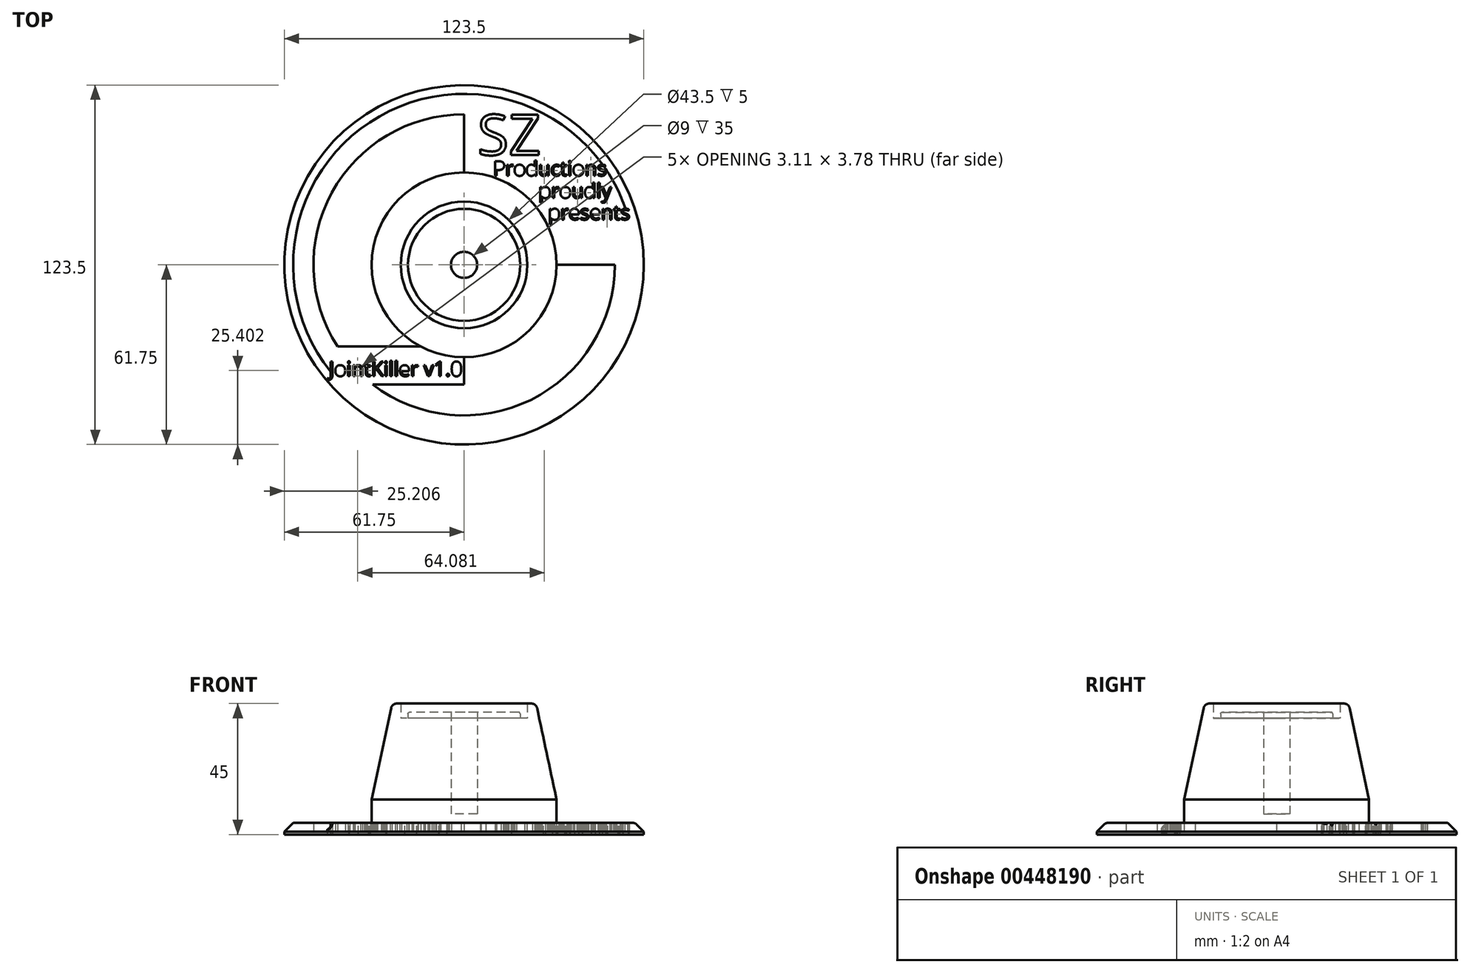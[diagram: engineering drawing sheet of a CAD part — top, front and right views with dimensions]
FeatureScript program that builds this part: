
annotation { "Feature Type Name" : "Feature", "Feature Type Description" : "" }
export const myFeature = defineFeature(function(context is Context, id is Id, definition is map)
    precondition{}
    {
        {
            var Q0;
            Q0=qCreatedBy(makeId("Top.planeOp"),FACE);
            var sketch = newSketch(context, id + "F0", { "sketchPlane" : qUnion([Q0])});
            skCircle(sketch, "E0", {"center": v(0, 0) * mm, "radius": 21.75 * mm});
            skCircle(sketch, "E1", {"center": v(0, 0) * mm, "radius": 19.25 * mm});
            skCircle(sketch, "E2", {"center": v(0, 0) * mm, "radius": 31.75 * mm});
            skCircle(sketch, "E3", {"center": v(0, 0) * mm, "radius": 61.75 * mm});
            skLineSegment(sketch, "E4", {"start": v(51.75, 0) * mm, "end": v(31.75, 0) * mm});
            skLineSegment(sketch, "E5", {"start": v(0, -51.75) * mm, "end": v(0, -31.75) * mm});
            skLineSegment(sketch, "E6", {"start": v(0, 51.75) * mm, "end": v(0, 31.75) * mm});
            skArc(sketch, "E7", {"start": v(-51.75, 0) * mm, "mid": v(-36.6, 36.6) * mm, "end": v(0, 51.75) * mm});
            skArc(sketch, "E8", {"start": v(51.75, 0) * mm, "mid": v(36.6, -36.6) * mm, "end": v(0, -51.75) * mm});
            skText(sketch, "E9", { "text": "JointKiller v1.0", "fontName": "OpenSans-Regular.ttf"});
            skCircle(sketch, "E10", {"center": v(0, 0) * mm, "radius": 4.5 * mm});
            skLineSegment(sketch, "E11.top", {"start": v(0, -41.13) * mm, "end": v(-31.4, -41.13) * mm});
            skLineSegment(sketch, "E11.left", {"start": v(0, -51.75) * mm, "end": v(0, -41.13) * mm});
            skText(sketch, "E12", { "text": "SZ", "fontName": "OpenSans-Regular.ttf"});
            skText(sketch, "E13", { "text": "Productions", "fontName": "OpenSans-Regular.ttf"});
            skText(sketch, "E14", { "text": "proudly", "fontName": "OpenSans-Regular.ttf"});
            skText(sketch, "E15", { "text": "presents\n", "fontName": "OpenSans-Regular.ttf"});
            skLineSegment(sketch, "E16.bottom", {"start": v(31.75, 0) * mm, "end": v(51.69, 0) * mm});
            skLineSegment(sketch, "E16.top", {"start": v(31.75, 12.81) * mm, "end": v(49.92, 12.81) * mm});
            skArc(sketch, "E17", {"start": v(-51.75, 0) * mm, "mid": v(-49.64, -14.61) * mm, "end": v(-43.5, -28.03) * mm});
            skLineSegment(sketch, "E18", {"start": v(31.75, 12.81) * mm, "end": v(29.05, 12.81) * mm});
            skArc(sketch, "E19", {"start": v(0, -51.75) * mm, "mid": v(-16.58, -49.02) * mm, "end": v(-31.4, -41.13) * mm});
            skArc(sketch, "E20", {"start": v(51.75, 0) * mm, "mid": v(51.35, 6.46) * mm, "end": v(50.14, 12.81) * mm});
            skLineSegment(sketch, "E21", {"start": v(-43.5, -28.03) * mm, "end": v(-14.9, -28.03) * mm});
            skLineSegment(sketch, "E22", {"start": v(0, -41.13) * mm, "end": v(22.58, -46.56) * mm});
            skLineSegment(sketch, "E23", {"start": v(28.12, -43.44) * mm, "end": v(26.04, -18.17) * mm});
            skLineSegment(sketch, "E24", {"start": v(23.6, -21.24) * mm, "end": v(22.4, -38.64) * mm});
            skLineSegment(sketch, "E25", {"start": v(22.4, -38.64) * mm, "end": v(0, -31.75) * mm});
            skLineSegment(sketch, "E26", {"start": v(-31.69, -2.02) * mm, "end": v(-51.75, 0) * mm});
            skLineSegment(sketch, "E27", {"start": v(-43.5, -28.03) * mm, "end": v(-30.77, -7.83) * mm});
            skLineSegment(sketch, "E28", {"start": v(-45.54, -24.58) * mm, "end": v(-40.29, -12.67) * mm});
            skLineSegment(sketch, "E29", {"start": v(-40.29, -12.67) * mm, "end": v(-51.15, -7.88) * mm});
            const initialGuessF0  = {"E9": [-0.0465, -0.03824, 1, 0, 0.005], "E12": [0.00463, 0.03773, 1, 0, 0.014], "E13": [0.00996, 0.03063, 1, 0, 0.005], "E14": [0.0256, 0.02298, 1, 0, 0.005], "E15": [0.0288, 0.01552, 1, 0, 0.005]};
            skSetInitialGuess(sketch, initialGuessF0);
            skSolve(sketch);
        }
        {
            var Q0;
            Q0 = qSketchRegion(id + "F0", true);
            extrude(context, id + "F1", {"entities" : qUnion([Q0]), "depth" : 4 * mm});
        }
        {
            var Q0;
            Q0=makeQuery(id+"F0.imprint","IMPRINT",FACE,{"disambiguationData":[TD([[makeQuery(id+"F0.imprint","IMPRINT",EDGE,{"derivedFrom":sQuery(id+"F0.wireOp",EDGE,"E0")}),-1.0]])]});
            extrude(context, id + "F2", {"entities" : qUnion([Q0]), "operationType" : NewBodyOperationType.ADD, "depth" : 45 * mm});
        }
        {
            var Q0;
            Q0=makeQuery(id+"F0.imprint","IMPRINT",FACE,{"disambiguationData":[TD([[makeQuery(id+"F0.imprint","IMPRINT",EDGE,{"derivedFrom":sQuery(id+"F0.wireOp",EDGE,"E0")}),1.0]])]});
            extrude(context, id + "F3", {"entities" : qUnion([Q0]), "operationType" : NewBodyOperationType.ADD, "depth" : 40 * mm});
        }
        {
            var Q0;
            Q0=makeQuery(id+"F0.imprint","IMPRINT",FACE,{"disambiguationData":[TD([[makeQuery(id+"F0.imprint","IMPRINT",EDGE,{"derivedFrom":sQuery(id+"F0.wireOp",EDGE,"E1")}),1.0]])]});
            extrude(context, id + "F4", {"entities" : qUnion([Q0]), "operationType" : NewBodyOperationType.ADD, "depth" : 42 * mm});
        }
        {
            var Q0;
            Q0=makeQuery(id+"F0.imprint","IMPRINT",FACE,{"disambiguationData":[TD([[makeQuery(id+"F0.imprint","IMPRINT",EDGE,{"derivedFrom":sQuery(id+"F0.wireOp",EDGE,"E10")}),1.0]])]});
            extrude(context, id + "F5", {"entities" : qUnion([Q0]), "operationType" : NewBodyOperationType.ADD, "depth" : 7 * mm});
        }
        {
            var Q0;
            Q0=makeQuery(id+"F2.opExtrude","CAP_EDGE",EDGE,{"disambiguationData":[OSD([sQuery(id+"F0.wireOp",EDGE,"E2")])],"isStart":false});
            chamfer(context, id + "F6", {"entities" : qUnion([Q0]), "chamferType" : ChamferType.OFFSET_ANGLE, "width" : 7 * mm, "oppositeDirection" : false, "angle" : 78 * degree, "tangentPropagation" : true});
        }
        {
            var Q0;
            {var subQ0=sQuery(id+"F0.wireOp",EDGE,"E2");Q0=makeQuery(id+"F6.opChamfer","BLEND_EDGE",EDGE,{"blendedFrom":[makeQuery(id+"F2.opExtrude","CAP_EDGE",EDGE,{"disambiguationData":[OSD([subQ0])],"isStart":false}),makeQuery(id+"F2.opExtrude","CAP_FACE",FACE,{"disambiguationData":[OSD([sQuery(id+"F0.wireOp",EDGE,"E0"),subQ0])],"isStart":false})],"blendedInto":[makeQuery(id+"F2.opExtrude","CAP_FACE",FACE,{"disambiguationData":[OSD([sQuery(id+"F0.wireOp",EDGE,"E0"),subQ0])],"isStart":false})]});}
            fillet(context, id + "F7", {"entities" : qUnion([Q0]), "radius" : 2 * mm, "tangentPropagation" : true, "allowEdgeOverflow" : false});
        }
        {
            var Q0;
            Q0=makeQuery(id+"F4.opExtrude","CAP_EDGE",EDGE,{"disambiguationData":[OSD([sQuery(id+"F0.wireOp",EDGE,"E1")])],"isStart":false});
            fillet(context, id + "F8", {"entities" : qUnion([Q0]), "radius" : 0.5 * mm, "tangentPropagation" : true, "allowEdgeOverflow" : false});
        }
        {
            var Q0;
            Q0=makeQuery(id+"F1.opExtrude","CAP_EDGE",EDGE,{"disambiguationData":[OSD([sQuery(id+"F0.wireOp",EDGE,"E3")])],"isStart":false});
            chamfer(context, id + "F9", {"entities" : qUnion([Q0]), "chamferType" : ChamferType.OFFSET_ANGLE, "width" : 3 * mm, "oppositeDirection" : false, "angle" : 45 * degree, "tangentPropagation" : true});
        }
        {
            var Q0;
            {var subQ0=sQuery(id+"F0.wireOp",EDGE,"E3");Q0=makeQuery(id+"F9.opChamfer","BLEND_EDGE",EDGE,{"disambiguationData":[OD(1.0)],"blendedFrom":[makeQuery(id+"F1.opExtrude","CAP_EDGE",EDGE,{"disambiguationData":[OSD([subQ0])],"isStart":false}),makeQuery(id+"F1.opExtrude","CAP_FACE",FACE,{"disambiguationData":[OSD([sQuery(id+"F0.wireOp",EDGE,"E2"),subQ0,sQuery(id+"F0.wireOp",EDGE,"E4"),sQuery(id+"F0.wireOp",EDGE,"E5"),sQuery(id+"F0.wireOp",EDGE,"E6"),sQuery(id+"F0.wireOp",EDGE,"E7"),sQuery(id+"F0.wireOp",EDGE,"E8"),sQuery(id+"F0.wireOp",EDGE,"E9.sketch_text.stroke-0"),sQuery(id+"F0.wireOp",EDGE,"E9.sketch_text.stroke-1"),sQuery(id+"F0.wireOp",EDGE,"E9.sketch_text.stroke-2"),sQuery(id+"F0.wireOp",EDGE,"E9.sketch_text.stroke-3"),sQuery(id+"F0.wireOp",EDGE,"E9.sketch_text.stroke-4"),sQuery(id+"F0.wireOp",EDGE,"E9.sketch_text.stroke-5"),sQuery(id+"F0.wireOp",EDGE,"E9.sketch_text.stroke-6"),sQuery(id+"F0.wireOp",EDGE,"E9.sketch_text.stroke-7"),sQuery(id+"F0.wireOp",EDGE,"E9.sketch_text.stroke-8"),sQuery(id+"F0.wireOp",EDGE,"E9.sketch_text.stroke-9"),sQuery(id+"F0.wireOp",EDGE,"E9.sketch_text.stroke-10"),sQuery(id+"F0.wireOp",EDGE,"E9.sketch_text.stroke-11"),sQuery(id+"F0.wireOp",EDGE,"E9.sketch_text.stroke-12"),sQuery(id+"F0.wireOp",EDGE,"E9.sketch_text.stroke-13"),sQuery(id+"F0.wireOp",EDGE,"E9.sketch_text.stroke-14"),sQuery(id+"F0.wireOp",EDGE,"E9.sketch_text.stroke-15"),sQuery(id+"F0.wireOp",EDGE,"E9.sketch_text.stroke-16"),sQuery(id+"F0.wireOp",EDGE,"E9.sketch_text.stroke-17"),sQuery(id+"F0.wireOp",EDGE,"E9.sketch_text.stroke-18"),sQuery(id+"F0.wireOp",EDGE,"E9.sketch_text.stroke-27"),sQuery(id+"F0.wireOp",EDGE,"E9.sketch_text.stroke-28"),sQuery(id+"F0.wireOp",EDGE,"E9.sketch_text.stroke-29"),sQuery(id+"F0.wireOp",EDGE,"E9.sketch_text.stroke-30"),sQuery(id+"F0.wireOp",EDGE,"E9.sketch_text.stroke-31"),sQuery(id+"F0.wireOp",EDGE,"E9.sketch_text.stroke-32"),sQuery(id+"F0.wireOp",EDGE,"E9.sketch_text.stroke-33"),sQuery(id+"F0.wireOp",EDGE,"E9.sketch_text.stroke-34"),sQuery(id+"F0.wireOp",EDGE,"E9.sketch_text.stroke-35"),sQuery(id+"F0.wireOp",EDGE,"E9.sketch_text.stroke-36"),sQuery(id+"F0.wireOp",EDGE,"E9.sketch_text.stroke-37"),sQuery(id+"F0.wireOp",EDGE,"E9.sketch_text.stroke-38"),sQuery(id+"F0.wireOp",EDGE,"E9.sketch_text.stroke-39"),sQuery(id+"F0.wireOp",EDGE,"E9.sketch_text.stroke-40"),sQuery(id+"F0.wireOp",EDGE,"E9.sketch_text.stroke-41"),sQuery(id+"F0.wireOp",EDGE,"E9.sketch_text.stroke-42"),sQuery(id+"F0.wireOp",EDGE,"E9.sketch_text.stroke-43"),sQuery(id+"F0.wireOp",EDGE,"E9.sketch_text.stroke-44"),sQuery(id+"F0.wireOp",EDGE,"E9.sketch_text.stroke-45"),sQuery(id+"F0.wireOp",EDGE,"E9.sketch_text.stroke-46"),sQuery(id+"F0.wireOp",EDGE,"E9.sketch_text.stroke-47"),sQuery(id+"F0.wireOp",EDGE,"E9.sketch_text.stroke-48"),sQuery(id+"F0.wireOp",EDGE,"E9.sketch_text.stroke-49"),sQuery(id+"F0.wireOp",EDGE,"E9.sketch_text.stroke-50"),sQuery(id+"F0.wireOp",EDGE,"E9.sketch_text.stroke-51"),sQuery(id+"F0.wireOp",EDGE,"E9.sketch_text.stroke-52"),sQuery(id+"F0.wireOp",EDGE,"E9.sketch_text.stroke-53"),sQuery(id+"F0.wireOp",EDGE,"E9.sketch_text.stroke-54"),sQuery(id+"F0.wireOp",EDGE,"E9.sketch_text.stroke-55"),sQuery(id+"F0.wireOp",EDGE,"E9.sketch_text.stroke-56"),sQuery(id+"F0.wireOp",EDGE,"E9.sketch_text.stroke-57"),sQuery(id+"F0.wireOp",EDGE,"E9.sketch_text.stroke-58"),sQuery(id+"F0.wireOp",EDGE,"E9.sketch_text.stroke-59"),sQuery(id+"F0.wireOp",EDGE,"E9.sketch_text.stroke-60"),sQuery(id+"F0.wireOp",EDGE,"E9.sketch_text.stroke-61"),sQuery(id+"F0.wireOp",EDGE,"E9.sketch_text.stroke-62"),sQuery(id+"F0.wireOp",EDGE,"E9.sketch_text.stroke-63"),sQuery(id+"F0.wireOp",EDGE,"E9.sketch_text.stroke-64"),sQuery(id+"F0.wireOp",EDGE,"E9.sketch_text.stroke-65"),sQuery(id+"F0.wireOp",EDGE,"E9.sketch_text.stroke-66"),sQuery(id+"F0.wireOp",EDGE,"E9.sketch_text.stroke-67"),sQuery(id+"F0.wireOp",EDGE,"E9.sketch_text.stroke-68"),sQuery(id+"F0.wireOp",EDGE,"E9.sketch_text.stroke-69"),sQuery(id+"F0.wireOp",EDGE,"E9.sketch_text.stroke-70"),sQuery(id+"F0.wireOp",EDGE,"E9.sketch_text.stroke-71"),sQuery(id+"F0.wireOp",EDGE,"E9.sketch_text.stroke-72"),sQuery(id+"F0.wireOp",EDGE,"E9.sketch_text.stroke-73"),sQuery(id+"F0.wireOp",EDGE,"E9.sketch_text.stroke-74"),sQuery(id+"F0.wireOp",EDGE,"E9.sketch_text.stroke-75"),sQuery(id+"F0.wireOp",EDGE,"E9.sketch_text.stroke-76"),sQuery(id+"F0.wireOp",EDGE,"E9.sketch_text.stroke-77"),sQuery(id+"F0.wireOp",EDGE,"E9.sketch_text.stroke-78"),sQuery(id+"F0.wireOp",EDGE,"E9.sketch_text.stroke-79"),sQuery(id+"F0.wireOp",EDGE,"E9.sketch_text.stroke-80"),sQuery(id+"F0.wireOp",EDGE,"E9.sketch_text.stroke-81"),sQuery(id+"F0.wireOp",EDGE,"E9.sketch_text.stroke-82"),sQuery(id+"F0.wireOp",EDGE,"E9.sketch_text.stroke-83"),sQuery(id+"F0.wireOp",EDGE,"E9.sketch_text.stroke-84"),sQuery(id+"F0.wireOp",EDGE,"E9.sketch_text.stroke-85"),sQuery(id+"F0.wireOp",EDGE,"E9.sketch_text.stroke-86"),sQuery(id+"F0.wireOp",EDGE,"E9.sketch_text.stroke-87"),sQuery(id+"F0.wireOp",EDGE,"E9.sketch_text.stroke-88"),sQuery(id+"F0.wireOp",EDGE,"E9.sketch_text.stroke-89"),sQuery(id+"F0.wireOp",EDGE,"E9.sketch_text.stroke-90"),sQuery(id+"F0.wireOp",EDGE,"E9.sketch_text.stroke-91"),sQuery(id+"F0.wireOp",EDGE,"E9.sketch_text.stroke-92"),sQuery(id+"F0.wireOp",EDGE,"E9.sketch_text.stroke-93"),sQuery(id+"F0.wireOp",EDGE,"E9.sketch_text.stroke-94"),sQuery(id+"F0.wireOp",EDGE,"E9.sketch_text.stroke-95"),sQuery(id+"F0.wireOp",EDGE,"E9.sketch_text.stroke-96"),sQuery(id+"F0.wireOp",EDGE,"E9.sketch_text.stroke-97"),sQuery(id+"F0.wireOp",EDGE,"E9.sketch_text.stroke-98"),sQuery(id+"F0.wireOp",EDGE,"E9.sketch_text.stroke-99"),sQuery(id+"F0.wireOp",EDGE,"E9.sketch_text.stroke-100"),sQuery(id+"F0.wireOp",EDGE,"E9.sketch_text.stroke-101"),sQuery(id+"F0.wireOp",EDGE,"E9.sketch_text.stroke-102"),sQuery(id+"F0.wireOp",EDGE,"E9.sketch_text.stroke-103"),sQuery(id+"F0.wireOp",EDGE,"E9.sketch_text.stroke-104"),sQuery(id+"F0.wireOp",EDGE,"E9.sketch_text.stroke-105"),sQuery(id+"F0.wireOp",EDGE,"E9.sketch_text.stroke-106"),sQuery(id+"F0.wireOp",EDGE,"E9.sketch_text.stroke-107"),sQuery(id+"F0.wireOp",EDGE,"E9.sketch_text.stroke-108"),sQuery(id+"F0.wireOp",EDGE,"E9.sketch_text.stroke-109"),sQuery(id+"F0.wireOp",EDGE,"E9.sketch_text.stroke-110"),sQuery(id+"F0.wireOp",EDGE,"E9.sketch_text.stroke-111"),sQuery(id+"F0.wireOp",EDGE,"E9.sketch_text.stroke-112"),sQuery(id+"F0.wireOp",EDGE,"E9.sketch_text.stroke-113"),sQuery(id+"F0.wireOp",EDGE,"E9.sketch_text.stroke-114"),sQuery(id+"F0.wireOp",EDGE,"E9.sketch_text.stroke-115"),sQuery(id+"F0.wireOp",EDGE,"E9.sketch_text.stroke-116"),sQuery(id+"F0.wireOp",EDGE,"E9.sketch_text.stroke-117"),sQuery(id+"F0.wireOp",EDGE,"E9.sketch_text.stroke-118"),sQuery(id+"F0.wireOp",EDGE,"E9.sketch_text.stroke-119"),sQuery(id+"F0.wireOp",EDGE,"E9.sketch_text.stroke-120"),sQuery(id+"F0.wireOp",EDGE,"E9.sketch_text.stroke-126"),sQuery(id+"F0.wireOp",EDGE,"E9.sketch_text.stroke-127"),sQuery(id+"F0.wireOp",EDGE,"E9.sketch_text.stroke-128"),sQuery(id+"F0.wireOp",EDGE,"E9.sketch_text.stroke-129"),sQuery(id+"F0.wireOp",EDGE,"E9.sketch_text.stroke-130"),sQuery(id+"F0.wireOp",EDGE,"E9.sketch_text.stroke-131"),sQuery(id+"F0.wireOp",EDGE,"E9.sketch_text.stroke-132"),sQuery(id+"F0.wireOp",EDGE,"E9.sketch_text.stroke-133"),sQuery(id+"F0.wireOp",EDGE,"E9.sketch_text.stroke-134"),sQuery(id+"F0.wireOp",EDGE,"E9.sketch_text.stroke-135"),sQuery(id+"F0.wireOp",EDGE,"E9.sketch_text.stroke-136"),sQuery(id+"F0.wireOp",EDGE,"E9.sketch_text.stroke-137"),sQuery(id+"F0.wireOp",EDGE,"E9.sketch_text.stroke-138"),sQuery(id+"F0.wireOp",EDGE,"E9.sketch_text.stroke-139"),sQuery(id+"F0.wireOp",EDGE,"E9.sketch_text.stroke-140"),sQuery(id+"F0.wireOp",EDGE,"E9.sketch_text.stroke-141"),sQuery(id+"F0.wireOp",EDGE,"E9.sketch_text.stroke-142"),sQuery(id+"F0.wireOp",EDGE,"E9.sketch_text.stroke-143"),sQuery(id+"F0.wireOp",EDGE,"E9.sketch_text.stroke-144"),sQuery(id+"F0.wireOp",EDGE,"E9.sketch_text.stroke-145"),sQuery(id+"F0.wireOp",EDGE,"E9.sketch_text.stroke-146"),sQuery(id+"F0.wireOp",EDGE,"E9.sketch_text.stroke-147"),sQuery(id+"F0.wireOp",EDGE,"E9.sketch_text.stroke-148"),sQuery(id+"F0.wireOp",EDGE,"E9.sketch_text.stroke-149"),sQuery(id+"F0.wireOp",EDGE,"E9.sketch_text.stroke-150"),sQuery(id+"F0.wireOp",EDGE,"E9.sketch_text.stroke-151"),sQuery(id+"F0.wireOp",EDGE,"E9.sketch_text.stroke-152"),sQuery(id+"F0.wireOp",EDGE,"E9.sketch_text.stroke-153"),sQuery(id+"F0.wireOp",EDGE,"E9.sketch_text.stroke-154"),sQuery(id+"F0.wireOp",EDGE,"E9.sketch_text.stroke-155"),sQuery(id+"F0.wireOp",EDGE,"E9.sketch_text.stroke-156"),sQuery(id+"F0.wireOp",EDGE,"E9.sketch_text.stroke-157"),sQuery(id+"F0.wireOp",EDGE,"E9.sketch_text.stroke-158"),sQuery(id+"F0.wireOp",EDGE,"E9.sketch_text.stroke-159"),sQuery(id+"F0.wireOp",EDGE,"E9.sketch_text.stroke-160"),sQuery(id+"F0.wireOp",EDGE,"E9.sketch_text.stroke-161"),sQuery(id+"F0.wireOp",EDGE,"E9.sketch_text.stroke-162"),sQuery(id+"F0.wireOp",EDGE,"E9.sketch_text.stroke-163"),sQuery(id+"F0.wireOp",EDGE,"E9.sketch_text.stroke-164"),sQuery(id+"F0.wireOp",EDGE,"E9.sketch_text.stroke-165"),sQuery(id+"F0.wireOp",EDGE,"E9.sketch_text.stroke-166"),sQuery(id+"F0.wireOp",EDGE,"E9.sketch_text.stroke-167"),sQuery(id+"F0.wireOp",EDGE,"E9.sketch_text.stroke-168"),sQuery(id+"F0.wireOp",EDGE,"E9.sketch_text.stroke-169"),sQuery(id+"F0.wireOp",EDGE,"E9.sketch_text.stroke-170"),sQuery(id+"F0.wireOp",EDGE,"E9.sketch_text.stroke-171"),sQuery(id+"F0.wireOp",EDGE,"E9.sketch_text.stroke-172"),sQuery(id+"F0.wireOp",EDGE,"E9.sketch_text.stroke-173"),sQuery(id+"F0.wireOp",EDGE,"E11.top"),sQuery(id+"F0.wireOp",EDGE,"E12.sketch_text.stroke-0"),sQuery(id+"F0.wireOp",EDGE,"E12.sketch_text.stroke-1"),sQuery(id+"F0.wireOp",EDGE,"E12.sketch_text.stroke-2"),sQuery(id+"F0.wireOp",EDGE,"E12.sketch_text.stroke-3"),sQuery(id+"F0.wireOp",EDGE,"E12.sketch_text.stroke-4"),sQuery(id+"F0.wireOp",EDGE,"E12.sketch_text.stroke-5"),sQuery(id+"F0.wireOp",EDGE,"E12.sketch_text.stroke-6"),sQuery(id+"F0.wireOp",EDGE,"E12.sketch_text.stroke-7"),sQuery(id+"F0.wireOp",EDGE,"E12.sketch_text.stroke-8"),sQuery(id+"F0.wireOp",EDGE,"E12.sketch_text.stroke-9"),sQuery(id+"F0.wireOp",EDGE,"E12.sketch_text.stroke-10"),sQuery(id+"F0.wireOp",EDGE,"E12.sketch_text.stroke-11"),sQuery(id+"F0.wireOp",EDGE,"E12.sketch_text.stroke-12"),sQuery(id+"F0.wireOp",EDGE,"E12.sketch_text.stroke-13"),sQuery(id+"F0.wireOp",EDGE,"E12.sketch_text.stroke-14"),sQuery(id+"F0.wireOp",EDGE,"E12.sketch_text.stroke-15"),sQuery(id+"F0.wireOp",EDGE,"E12.sketch_text.stroke-16"),sQuery(id+"F0.wireOp",EDGE,"E12.sketch_text.stroke-17"),sQuery(id+"F0.wireOp",EDGE,"E12.sketch_text.stroke-18"),sQuery(id+"F0.wireOp",EDGE,"E12.sketch_text.stroke-19"),sQuery(id+"F0.wireOp",EDGE,"E12.sketch_text.stroke-20"),sQuery(id+"F0.wireOp",EDGE,"E12.sketch_text.stroke-21"),sQuery(id+"F0.wireOp",EDGE,"E12.sketch_text.stroke-22"),sQuery(id+"F0.wireOp",EDGE,"E12.sketch_text.stroke-23"),sQuery(id+"F0.wireOp",EDGE,"E12.sketch_text.stroke-24"),sQuery(id+"F0.wireOp",EDGE,"E12.sketch_text.stroke-25"),sQuery(id+"F0.wireOp",EDGE,"E12.sketch_text.stroke-26"),sQuery(id+"F0.wireOp",EDGE,"E12.sketch_text.stroke-27"),sQuery(id+"F0.wireOp",EDGE,"E12.sketch_text.stroke-28"),sQuery(id+"F0.wireOp",EDGE,"E12.sketch_text.stroke-29"),sQuery(id+"F0.wireOp",EDGE,"E12.sketch_text.stroke-30"),sQuery(id+"F0.wireOp",EDGE,"E12.sketch_text.stroke-31"),sQuery(id+"F0.wireOp",EDGE,"E12.sketch_text.stroke-32"),sQuery(id+"F0.wireOp",EDGE,"E12.sketch_text.stroke-33"),sQuery(id+"F0.wireOp",EDGE,"E12.sketch_text.stroke-34"),sQuery(id+"F0.wireOp",EDGE,"E13.sketch_text.stroke-0"),sQuery(id+"F0.wireOp",EDGE,"E13.sketch_text.stroke-1"),sQuery(id+"F0.wireOp",EDGE,"E13.sketch_text.stroke-2"),sQuery(id+"F0.wireOp",EDGE,"E13.sketch_text.stroke-3"),sQuery(id+"F0.wireOp",EDGE,"E13.sketch_text.stroke-4"),sQuery(id+"F0.wireOp",EDGE,"E13.sketch_text.stroke-5"),sQuery(id+"F0.wireOp",EDGE,"E13.sketch_text.stroke-6"),sQuery(id+"F0.wireOp",EDGE,"E13.sketch_text.stroke-7"),sQuery(id+"F0.wireOp",EDGE,"E13.sketch_text.stroke-15"),sQuery(id+"F0.wireOp",EDGE,"E13.sketch_text.stroke-16"),sQuery(id+"F0.wireOp",EDGE,"E13.sketch_text.stroke-17"),sQuery(id+"F0.wireOp",EDGE,"E13.sketch_text.stroke-18"),sQuery(id+"F0.wireOp",EDGE,"E13.sketch_text.stroke-19"),sQuery(id+"F0.wireOp",EDGE,"E13.sketch_text.stroke-20"),sQuery(id+"F0.wireOp",EDGE,"E13.sketch_text.stroke-21"),sQuery(id+"F0.wireOp",EDGE,"E13.sketch_text.stroke-22"),sQuery(id+"F0.wireOp",EDGE,"E13.sketch_text.stroke-23"),sQuery(id+"F0.wireOp",EDGE,"E13.sketch_text.stroke-24"),sQuery(id+"F0.wireOp",EDGE,"E13.sketch_text.stroke-25"),sQuery(id+"F0.wireOp",EDGE,"E13.sketch_text.stroke-26"),sQuery(id+"F0.wireOp",EDGE,"E13.sketch_text.stroke-27"),sQuery(id+"F0.wireOp",EDGE,"E13.sketch_text.stroke-28"),sQuery(id+"F0.wireOp",EDGE,"E13.sketch_text.stroke-29"),sQuery(id+"F0.wireOp",EDGE,"E13.sketch_text.stroke-30"),sQuery(id+"F0.wireOp",EDGE,"E13.sketch_text.stroke-31"),sQuery(id+"F0.wireOp",EDGE,"E13.sketch_text.stroke-32"),sQuery(id+"F0.wireOp",EDGE,"E13.sketch_text.stroke-33"),sQuery(id+"F0.wireOp",EDGE,"E13.sketch_text.stroke-34"),sQuery(id+"F0.wireOp",EDGE,"E13.sketch_text.stroke-35"),sQuery(id+"F0.wireOp",EDGE,"E13.sketch_text.stroke-36"),sQuery(id+"F0.wireOp",EDGE,"E13.sketch_text.stroke-45"),sQuery(id+"F0.wireOp",EDGE,"E13.sketch_text.stroke-46"),sQuery(id+"F0.wireOp",EDGE,"E13.sketch_text.stroke-47"),sQuery(id+"F0.wireOp",EDGE,"E13.sketch_text.stroke-48"),sQuery(id+"F0.wireOp",EDGE,"E13.sketch_text.stroke-49"),sQuery(id+"F0.wireOp",EDGE,"E13.sketch_text.stroke-50"),sQuery(id+"F0.wireOp",EDGE,"E13.sketch_text.stroke-51"),sQuery(id+"F0.wireOp",EDGE,"E13.sketch_text.stroke-52"),sQuery(id+"F0.wireOp",EDGE,"E13.sketch_text.stroke-53"),sQuery(id+"F0.wireOp",EDGE,"E13.sketch_text.stroke-54"),sQuery(id+"F0.wireOp",EDGE,"E13.sketch_text.stroke-55"),sQuery(id+"F0.wireOp",EDGE,"E13.sketch_text.stroke-56"),sQuery(id+"F0.wireOp",EDGE,"E13.sketch_text.stroke-57"),sQuery(id+"F0.wireOp",EDGE,"E13.sketch_text.stroke-58"),sQuery(id+"F0.wireOp",EDGE,"E13.sketch_text.stroke-59"),sQuery(id+"F0.wireOp",EDGE,"E13.sketch_text.stroke-69"),sQuery(id+"F0.wireOp",EDGE,"E13.sketch_text.stroke-70"),sQuery(id+"F0.wireOp",EDGE,"E13.sketch_text.stroke-71"),sQuery(id+"F0.wireOp",EDGE,"E13.sketch_text.stroke-72"),sQuery(id+"F0.wireOp",EDGE,"E13.sketch_text.stroke-73"),sQuery(id+"F0.wireOp",EDGE,"E13.sketch_text.stroke-74"),sQuery(id+"F0.wireOp",EDGE,"E13.sketch_text.stroke-75"),sQuery(id+"F0.wireOp",EDGE,"E13.sketch_text.stroke-76"),sQuery(id+"F0.wireOp",EDGE,"E13.sketch_text.stroke-77"),sQuery(id+"F0.wireOp",EDGE,"E13.sketch_text.stroke-78"),sQuery(id+"F0.wireOp",EDGE,"E13.sketch_text.stroke-79"),sQuery(id+"F0.wireOp",EDGE,"E13.sketch_text.stroke-80"),sQuery(id+"F0.wireOp",EDGE,"E13.sketch_text.stroke-81"),sQuery(id+"F0.wireOp",EDGE,"E13.sketch_text.stroke-82"),sQuery(id+"F0.wireOp",EDGE,"E13.sketch_text.stroke-83"),sQuery(id+"F0.wireOp",EDGE,"E13.sketch_text.stroke-84"),sQuery(id+"F0.wireOp",EDGE,"E13.sketch_text.stroke-85"),sQuery(id+"F0.wireOp",EDGE,"E13.sketch_text.stroke-86"),sQuery(id+"F0.wireOp",EDGE,"E13.sketch_text.stroke-87"),sQuery(id+"F0.wireOp",EDGE,"E13.sketch_text.stroke-88"),sQuery(id+"F0.wireOp",EDGE,"E13.sketch_text.stroke-89"),sQuery(id+"F0.wireOp",EDGE,"E13.sketch_text.stroke-90"),sQuery(id+"F0.wireOp",EDGE,"E13.sketch_text.stroke-91"),sQuery(id+"F0.wireOp",EDGE,"E13.sketch_text.stroke-92"),sQuery(id+"F0.wireOp",EDGE,"E13.sketch_text.stroke-93"),sQuery(id+"F0.wireOp",EDGE,"E13.sketch_text.stroke-94"),sQuery(id+"F0.wireOp",EDGE,"E13.sketch_text.stroke-95"),sQuery(id+"F0.wireOp",EDGE,"E13.sketch_text.stroke-96"),sQuery(id+"F0.wireOp",EDGE,"E13.sketch_text.stroke-97"),sQuery(id+"F0.wireOp",EDGE,"E13.sketch_text.stroke-98"),sQuery(id+"F0.wireOp",EDGE,"E13.sketch_text.stroke-99"),sQuery(id+"F0.wireOp",EDGE,"E13.sketch_text.stroke-100"),sQuery(id+"F0.wireOp",EDGE,"E13.sketch_text.stroke-101"),sQuery(id+"F0.wireOp",EDGE,"E13.sketch_text.stroke-102"),sQuery(id+"F0.wireOp",EDGE,"E13.sketch_text.stroke-103"),sQuery(id+"F0.wireOp",EDGE,"E13.sketch_text.stroke-104"),sQuery(id+"F0.wireOp",EDGE,"E13.sketch_text.stroke-105"),sQuery(id+"F0.wireOp",EDGE,"E13.sketch_text.stroke-106"),sQuery(id+"F0.wireOp",EDGE,"E13.sketch_text.stroke-107"),sQuery(id+"F0.wireOp",EDGE,"E13.sketch_text.stroke-108"),sQuery(id+"F0.wireOp",EDGE,"E13.sketch_text.stroke-109"),sQuery(id+"F0.wireOp",EDGE,"E13.sketch_text.stroke-110"),sQuery(id+"F0.wireOp",EDGE,"E13.sketch_text.stroke-111"),sQuery(id+"F0.wireOp",EDGE,"E13.sketch_text.stroke-112"),sQuery(id+"F0.wireOp",EDGE,"E13.sketch_text.stroke-113"),sQuery(id+"F0.wireOp",EDGE,"E13.sketch_text.stroke-114"),sQuery(id+"F0.wireOp",EDGE,"E13.sketch_text.stroke-115"),sQuery(id+"F0.wireOp",EDGE,"E13.sketch_text.stroke-116"),sQuery(id+"F0.wireOp",EDGE,"E13.sketch_text.stroke-117"),sQuery(id+"F0.wireOp",EDGE,"E13.sketch_text.stroke-118"),sQuery(id+"F0.wireOp",EDGE,"E13.sketch_text.stroke-119"),sQuery(id+"F0.wireOp",EDGE,"E13.sketch_text.stroke-120"),sQuery(id+"F0.wireOp",EDGE,"E13.sketch_text.stroke-121"),sQuery(id+"F0.wireOp",EDGE,"E13.sketch_text.stroke-122"),sQuery(id+"F0.wireOp",EDGE,"E13.sketch_text.stroke-123"),sQuery(id+"F0.wireOp",EDGE,"E13.sketch_text.stroke-124"),sQuery(id+"F0.wireOp",EDGE,"E13.sketch_text.stroke-125"),sQuery(id+"F0.wireOp",EDGE,"E13.sketch_text.stroke-126"),sQuery(id+"F0.wireOp",EDGE,"E13.sketch_text.stroke-127"),sQuery(id+"F0.wireOp",EDGE,"E13.sketch_text.stroke-128"),sQuery(id+"F0.wireOp",EDGE,"E13.sketch_text.stroke-129"),sQuery(id+"F0.wireOp",EDGE,"E13.sketch_text.stroke-130"),sQuery(id+"F0.wireOp",EDGE,"E13.sketch_text.stroke-131"),sQuery(id+"F0.wireOp",EDGE,"E13.sketch_text.stroke-132"),sQuery(id+"F0.wireOp",EDGE,"E13.sketch_text.stroke-133"),sQuery(id+"F0.wireOp",EDGE,"E13.sketch_text.stroke-134"),sQuery(id+"F0.wireOp",EDGE,"E13.sketch_text.stroke-135"),sQuery(id+"F0.wireOp",EDGE,"E13.sketch_text.stroke-136"),sQuery(id+"F0.wireOp",EDGE,"E13.sketch_text.stroke-137"),sQuery(id+"F0.wireOp",EDGE,"E13.sketch_text.stroke-138"),sQuery(id+"F0.wireOp",EDGE,"E13.sketch_text.stroke-139"),sQuery(id+"F0.wireOp",EDGE,"E13.sketch_text.stroke-140"),sQuery(id+"F0.wireOp",EDGE,"E13.sketch_text.stroke-149"),sQuery(id+"F0.wireOp",EDGE,"E13.sketch_text.stroke-150"),sQuery(id+"F0.wireOp",EDGE,"E13.sketch_text.stroke-151"),sQuery(id+"F0.wireOp",EDGE,"E13.sketch_text.stroke-152"),sQuery(id+"F0.wireOp",EDGE,"E13.sketch_text.stroke-153"),sQuery(id+"F0.wireOp",EDGE,"E13.sketch_text.stroke-154"),sQuery(id+"F0.wireOp",EDGE,"E13.sketch_text.stroke-155"),sQuery(id+"F0.wireOp",EDGE,"E13.sketch_text.stroke-156"),sQuery(id+"F0.wireOp",EDGE,"E13.sketch_text.stroke-157"),sQuery(id+"F0.wireOp",EDGE,"E13.sketch_text.stroke-158"),sQuery(id+"F0.wireOp",EDGE,"E13.sketch_text.stroke-159"),sQuery(id+"F0.wireOp",EDGE,"E13.sketch_text.stroke-160"),sQuery(id+"F0.wireOp",EDGE,"E13.sketch_text.stroke-161"),sQuery(id+"F0.wireOp",EDGE,"E13.sketch_text.stroke-162"),sQuery(id+"F0.wireOp",EDGE,"E13.sketch_text.stroke-163"),sQuery(id+"F0.wireOp",EDGE,"E13.sketch_text.stroke-164"),sQuery(id+"F0.wireOp",EDGE,"E13.sketch_text.stroke-165"),sQuery(id+"F0.wireOp",EDGE,"E13.sketch_text.stroke-166"),sQuery(id+"F0.wireOp",EDGE,"E13.sketch_text.stroke-167"),sQuery(id+"F0.wireOp",EDGE,"E13.sketch_text.stroke-168"),sQuery(id+"F0.wireOp",EDGE,"E13.sketch_text.stroke-169"),sQuery(id+"F0.wireOp",EDGE,"E13.sketch_text.stroke-170"),sQuery(id+"F0.wireOp",EDGE,"E13.sketch_text.stroke-171"),sQuery(id+"F0.wireOp",EDGE,"E13.sketch_text.stroke-172"),sQuery(id+"F0.wireOp",EDGE,"E13.sketch_text.stroke-173"),sQuery(id+"F0.wireOp",EDGE,"E13.sketch_text.stroke-174"),sQuery(id+"F0.wireOp",EDGE,"E13.sketch_text.stroke-175"),sQuery(id+"F0.wireOp",EDGE,"E13.sketch_text.stroke-176"),sQuery(id+"F0.wireOp",EDGE,"E13.sketch_text.stroke-177"),sQuery(id+"F0.wireOp",EDGE,"E13.sketch_text.stroke-178"),sQuery(id+"F0.wireOp",EDGE,"E13.sketch_text.stroke-179"),sQuery(id+"F0.wireOp",EDGE,"E13.sketch_text.stroke-180"),sQuery(id+"F0.wireOp",EDGE,"E13.sketch_text.stroke-181"),sQuery(id+"F0.wireOp",EDGE,"E13.sketch_text.stroke-182"),sQuery(id+"F0.wireOp",EDGE,"E13.sketch_text.stroke-183"),sQuery(id+"F0.wireOp",EDGE,"E13.sketch_text.stroke-184"),sQuery(id+"F0.wireOp",EDGE,"E13.sketch_text.stroke-185"),sQuery(id+"F0.wireOp",EDGE,"E13.sketch_text.stroke-186"),sQuery(id+"F0.wireOp",EDGE,"E13.sketch_text.stroke-187"),sQuery(id+"F0.wireOp",EDGE,"E13.sketch_text.stroke-188"),sQuery(id+"F0.wireOp",EDGE,"E13.sketch_text.stroke-189"),sQuery(id+"F0.wireOp",EDGE,"E13.sketch_text.stroke-190"),sQuery(id+"F0.wireOp",EDGE,"E14.sketch_text.stroke-0"),sQuery(id+"F0.wireOp",EDGE,"E14.sketch_text.stroke-1"),sQuery(id+"F0.wireOp",EDGE,"E14.sketch_text.stroke-2"),sQuery(id+"F0.wireOp",EDGE,"E14.sketch_text.stroke-3"),sQuery(id+"F0.wireOp",EDGE,"E14.sketch_text.stroke-4"),sQuery(id+"F0.wireOp",EDGE,"E14.sketch_text.stroke-5"),sQuery(id+"F0.wireOp",EDGE,"E14.sketch_text.stroke-6"),sQuery(id+"F0.wireOp",EDGE,"E14.sketch_text.stroke-7"),sQuery(id+"F0.wireOp",EDGE,"E14.sketch_text.stroke-8"),sQuery(id+"F0.wireOp",EDGE,"E14.sketch_text.stroke-9"),sQuery(id+"F0.wireOp",EDGE,"E14.sketch_text.stroke-10"),sQuery(id+"F0.wireOp",EDGE,"E14.sketch_text.stroke-11"),sQuery(id+"F0.wireOp",EDGE,"E14.sketch_text.stroke-12"),sQuery(id+"F0.wireOp",EDGE,"E14.sketch_text.stroke-13"),sQuery(id+"F0.wireOp",EDGE,"E14.sketch_text.stroke-14"),sQuery(id+"F0.wireOp",EDGE,"E14.sketch_text.stroke-15"),sQuery(id+"F0.wireOp",EDGE,"E14.sketch_text.stroke-25"),sQuery(id+"F0.wireOp",EDGE,"E14.sketch_text.stroke-26"),sQuery(id+"F0.wireOp",EDGE,"E14.sketch_text.stroke-27"),sQuery(id+"F0.wireOp",EDGE,"E14.sketch_text.stroke-28"),sQuery(id+"F0.wireOp",EDGE,"E14.sketch_text.stroke-29"),sQuery(id+"F0.wireOp",EDGE,"E14.sketch_text.stroke-30"),sQuery(id+"F0.wireOp",EDGE,"E14.sketch_text.stroke-31"),sQuery(id+"F0.wireOp",EDGE,"E14.sketch_text.stroke-32"),sQuery(id+"F0.wireOp",EDGE,"E14.sketch_text.stroke-33"),sQuery(id+"F0.wireOp",EDGE,"E14.sketch_text.stroke-34"),sQuery(id+"F0.wireOp",EDGE,"E14.sketch_text.stroke-35"),sQuery(id+"F0.wireOp",EDGE,"E14.sketch_text.stroke-36"),sQuery(id+"F0.wireOp",EDGE,"E14.sketch_text.stroke-37"),sQuery(id+"F0.wireOp",EDGE,"E14.sketch_text.stroke-38"),sQuery(id+"F0.wireOp",EDGE,"E14.sketch_text.stroke-39"),sQuery(id+"F0.wireOp",EDGE,"E14.sketch_text.stroke-40"),sQuery(id+"F0.wireOp",EDGE,"E14.sketch_text.stroke-41"),sQuery(id+"F0.wireOp",EDGE,"E14.sketch_text.stroke-42"),sQuery(id+"F0.wireOp",EDGE,"E14.sketch_text.stroke-43"),sQuery(id+"F0.wireOp",EDGE,"E14.sketch_text.stroke-44"),sQuery(id+"F0.wireOp",EDGE,"E14.sketch_text.stroke-45"),sQuery(id+"F0.wireOp",EDGE,"E14.sketch_text.stroke-46"),sQuery(id+"F0.wireOp",EDGE,"E14.sketch_text.stroke-55"),sQuery(id+"F0.wireOp",EDGE,"E14.sketch_text.stroke-56"),sQuery(id+"F0.wireOp",EDGE,"E14.sketch_text.stroke-57"),sQuery(id+"F0.wireOp",EDGE,"E14.sketch_text.stroke-58"),sQuery(id+"F0.wireOp",EDGE,"E14.sketch_text.stroke-59"),sQuery(id+"F0.wireOp",EDGE,"E14.sketch_text.stroke-60"),sQuery(id+"F0.wireOp",EDGE,"E14.sketch_text.stroke-61"),sQuery(id+"F0.wireOp",EDGE,"E14.sketch_text.stroke-62"),sQuery(id+"F0.wireOp",EDGE,"E14.sketch_text.stroke-63"),sQuery(id+"F0.wireOp",EDGE,"E14.sketch_text.stroke-64"),sQuery(id+"F0.wireOp",EDGE,"E14.sketch_text.stroke-65"),sQuery(id+"F0.wireOp",EDGE,"E14.sketch_text.stroke-66"),sQuery(id+"F0.wireOp",EDGE,"E14.sketch_text.stroke-67"),sQuery(id+"F0.wireOp",EDGE,"E14.sketch_text.stroke-68"),sQuery(id+"F0.wireOp",EDGE,"E14.sketch_text.stroke-69"),sQuery(id+"F0.wireOp",EDGE,"E14.sketch_text.stroke-70"),sQuery(id+"F0.wireOp",EDGE,"E14.sketch_text.stroke-71"),sQuery(id+"F0.wireOp",EDGE,"E14.sketch_text.stroke-72"),sQuery(id+"F0.wireOp",EDGE,"E14.sketch_text.stroke-73"),sQuery(id+"F0.wireOp",EDGE,"E14.sketch_text.stroke-74"),sQuery(id+"F0.wireOp",EDGE,"E14.sketch_text.stroke-75"),sQuery(id+"F0.wireOp",EDGE,"E14.sketch_text.stroke-76"),sQuery(id+"F0.wireOp",EDGE,"E14.sketch_text.stroke-77"),sQuery(id+"F0.wireOp",EDGE,"E14.sketch_text.stroke-78"),sQuery(id+"F0.wireOp",EDGE,"E14.sketch_text.stroke-79"),sQuery(id+"F0.wireOp",EDGE,"E14.sketch_text.stroke-80"),sQuery(id+"F0.wireOp",EDGE,"E14.sketch_text.stroke-81"),sQuery(id+"F0.wireOp",EDGE,"E14.sketch_text.stroke-82"),sQuery(id+"F0.wireOp",EDGE,"E14.sketch_text.stroke-83"),sQuery(id+"F0.wireOp",EDGE,"E14.sketch_text.stroke-84"),sQuery(id+"F0.wireOp",EDGE,"E14.sketch_text.stroke-85"),sQuery(id+"F0.wireOp",EDGE,"E14.sketch_text.stroke-86"),sQuery(id+"F0.wireOp",EDGE,"E14.sketch_text.stroke-96"),sQuery(id+"F0.wireOp",EDGE,"E14.sketch_text.stroke-97"),sQuery(id+"F0.wireOp",EDGE,"E14.sketch_text.stroke-98"),sQuery(id+"F0.wireOp",EDGE,"E14.sketch_text.stroke-99"),sQuery(id+"F0.wireOp",EDGE,"E14.sketch_text.stroke-100"),sQuery(id+"F0.wireOp",EDGE,"E14.sketch_text.stroke-101"),sQuery(id+"F0.wireOp",EDGE,"E14.sketch_text.stroke-102"),sQuery(id+"F0.wireOp",EDGE,"E14.sketch_text.stroke-103"),sQuery(id+"F0.wireOp",EDGE,"E14.sketch_text.stroke-104"),sQuery(id+"F0.wireOp",EDGE,"E14.sketch_text.stroke-105"),sQuery(id+"F0.wireOp",EDGE,"E14.sketch_text.stroke-106"),sQuery(id+"F0.wireOp",EDGE,"E14.sketch_text.stroke-107"),sQuery(id+"F0.wireOp",EDGE,"E14.sketch_text.stroke-108"),sQuery(id+"F0.wireOp",EDGE,"E14.sketch_text.stroke-109"),sQuery(id+"F0.wireOp",EDGE,"E14.sketch_text.stroke-110"),sQuery(id+"F0.wireOp",EDGE,"E14.sketch_text.stroke-111"),sQuery(id+"F0.wireOp",EDGE,"E14.sketch_text.stroke-112"),sQuery(id+"F0.wireOp",EDGE,"E14.sketch_text.stroke-113"),sQuery(id+"F0.wireOp",EDGE,"E14.sketch_text.stroke-114"),sQuery(id+"F0.wireOp",EDGE,"E14.sketch_text.stroke-115"),sQuery(id+"F0.wireOp",EDGE,"E15.sketch_text.stroke-0"),sQuery(id+"F0.wireOp",EDGE,"E15.sketch_text.stroke-1"),sQuery(id+"F0.wireOp",EDGE,"E15.sketch_text.stroke-2"),sQuery(id+"F0.wireOp",EDGE,"E15.sketch_text.stroke-3"),sQuery(id+"F0.wireOp",EDGE,"E15.sketch_text.stroke-4"),sQuery(id+"F0.wireOp",EDGE,"E15.sketch_text.stroke-5"),sQuery(id+"F0.wireOp",EDGE,"E15.sketch_text.stroke-6"),sQuery(id+"F0.wireOp",EDGE,"E15.sketch_text.stroke-7"),sQuery(id+"F0.wireOp",EDGE,"E15.sketch_text.stroke-8"),sQuery(id+"F0.wireOp",EDGE,"E15.sketch_text.stroke-9"),sQuery(id+"F0.wireOp",EDGE,"E15.sketch_text.stroke-10"),sQuery(id+"F0.wireOp",EDGE,"E15.sketch_text.stroke-11"),sQuery(id+"F0.wireOp",EDGE,"E15.sketch_text.stroke-12"),sQuery(id+"F0.wireOp",EDGE,"E15.sketch_text.stroke-13"),sQuery(id+"F0.wireOp",EDGE,"E15.sketch_text.stroke-14"),sQuery(id+"F0.wireOp",EDGE,"E15.sketch_text.stroke-15"),sQuery(id+"F0.wireOp",EDGE,"E15.sketch_text.stroke-25"),sQuery(id+"F0.wireOp",EDGE,"E15.sketch_text.stroke-26"),sQuery(id+"F0.wireOp",EDGE,"E15.sketch_text.stroke-27"),sQuery(id+"F0.wireOp",EDGE,"E15.sketch_text.stroke-28"),sQuery(id+"F0.wireOp",EDGE,"E15.sketch_text.stroke-29"),sQuery(id+"F0.wireOp",EDGE,"E15.sketch_text.stroke-30"),sQuery(id+"F0.wireOp",EDGE,"E15.sketch_text.stroke-31"),sQuery(id+"F0.wireOp",EDGE,"E15.sketch_text.stroke-32"),sQuery(id+"F0.wireOp",EDGE,"E15.sketch_text.stroke-33"),sQuery(id+"F0.wireOp",EDGE,"E15.sketch_text.stroke-34"),sQuery(id+"F0.wireOp",EDGE,"E15.sketch_text.stroke-35"),sQuery(id+"F0.wireOp",EDGE,"E15.sketch_text.stroke-36"),sQuery(id+"F0.wireOp",EDGE,"E15.sketch_text.stroke-37"),sQuery(id+"F0.wireOp",EDGE,"E15.sketch_text.stroke-38"),sQuery(id+"F0.wireOp",EDGE,"E15.sketch_text.stroke-39"),sQuery(id+"F0.wireOp",EDGE,"E15.sketch_text.stroke-40"),sQuery(id+"F0.wireOp",EDGE,"E15.sketch_text.stroke-41"),sQuery(id+"F0.wireOp",EDGE,"E15.sketch_text.stroke-42"),sQuery(id+"F0.wireOp",EDGE,"E15.sketch_text.stroke-43"),sQuery(id+"F0.wireOp",EDGE,"E15.sketch_text.stroke-44"),sQuery(id+"F0.wireOp",EDGE,"E15.sketch_text.stroke-45"),sQuery(id+"F0.wireOp",EDGE,"E15.sketch_text.stroke-46"),sQuery(id+"F0.wireOp",EDGE,"E15.sketch_text.stroke-47"),sQuery(id+"F0.wireOp",EDGE,"E15.sketch_text.stroke-48"),sQuery(id+"F0.wireOp",EDGE,"E15.sketch_text.stroke-49"),sQuery(id+"F0.wireOp",EDGE,"E15.sketch_text.stroke-50"),sQuery(id+"F0.wireOp",EDGE,"E15.sketch_text.stroke-51"),sQuery(id+"F0.wireOp",EDGE,"E15.sketch_text.stroke-57"),sQuery(id+"F0.wireOp",EDGE,"E15.sketch_text.stroke-58"),sQuery(id+"F0.wireOp",EDGE,"E15.sketch_text.stroke-59"),sQuery(id+"F0.wireOp",EDGE,"E15.sketch_text.stroke-60"),sQuery(id+"F0.wireOp",EDGE,"E15.sketch_text.stroke-61"),sQuery(id+"F0.wireOp",EDGE,"E15.sketch_text.stroke-62"),sQuery(id+"F0.wireOp",EDGE,"E15.sketch_text.stroke-63"),sQuery(id+"F0.wireOp",EDGE,"E15.sketch_text.stroke-64"),sQuery(id+"F0.wireOp",EDGE,"E15.sketch_text.stroke-65"),sQuery(id+"F0.wireOp",EDGE,"E15.sketch_text.stroke-66"),sQuery(id+"F0.wireOp",EDGE,"E15.sketch_text.stroke-67"),sQuery(id+"F0.wireOp",EDGE,"E15.sketch_text.stroke-68"),sQuery(id+"F0.wireOp",EDGE,"E15.sketch_text.stroke-69"),sQuery(id+"F0.wireOp",EDGE,"E15.sketch_text.stroke-70"),sQuery(id+"F0.wireOp",EDGE,"E15.sketch_text.stroke-71"),sQuery(id+"F0.wireOp",EDGE,"E15.sketch_text.stroke-72"),sQuery(id+"F0.wireOp",EDGE,"E15.sketch_text.stroke-73"),sQuery(id+"F0.wireOp",EDGE,"E15.sketch_text.stroke-74"),sQuery(id+"F0.wireOp",EDGE,"E15.sketch_text.stroke-75"),sQuery(id+"F0.wireOp",EDGE,"E15.sketch_text.stroke-76"),sQuery(id+"F0.wireOp",EDGE,"E15.sketch_text.stroke-77"),sQuery(id+"F0.wireOp",EDGE,"E15.sketch_text.stroke-78"),sQuery(id+"F0.wireOp",EDGE,"E15.sketch_text.stroke-79"),sQuery(id+"F0.wireOp",EDGE,"E15.sketch_text.stroke-80"),sQuery(id+"F0.wireOp",EDGE,"E15.sketch_text.stroke-81"),sQuery(id+"F0.wireOp",EDGE,"E15.sketch_text.stroke-82"),sQuery(id+"F0.wireOp",EDGE,"E15.sketch_text.stroke-83"),sQuery(id+"F0.wireOp",EDGE,"E15.sketch_text.stroke-84"),sQuery(id+"F0.wireOp",EDGE,"E15.sketch_text.stroke-85"),sQuery(id+"F0.wireOp",EDGE,"E15.sketch_text.stroke-86"),sQuery(id+"F0.wireOp",EDGE,"E15.sketch_text.stroke-87"),sQuery(id+"F0.wireOp",EDGE,"E15.sketch_text.stroke-88"),sQuery(id+"F0.wireOp",EDGE,"E15.sketch_text.stroke-89"),sQuery(id+"F0.wireOp",EDGE,"E15.sketch_text.stroke-90"),sQuery(id+"F0.wireOp",EDGE,"E15.sketch_text.stroke-91"),sQuery(id+"F0.wireOp",EDGE,"E15.sketch_text.stroke-92"),sQuery(id+"F0.wireOp",EDGE,"E15.sketch_text.stroke-93"),sQuery(id+"F0.wireOp",EDGE,"E15.sketch_text.stroke-94"),sQuery(id+"F0.wireOp",EDGE,"E15.sketch_text.stroke-95"),sQuery(id+"F0.wireOp",EDGE,"E15.sketch_text.stroke-101"),sQuery(id+"F0.wireOp",EDGE,"E15.sketch_text.stroke-102"),sQuery(id+"F0.wireOp",EDGE,"E15.sketch_text.stroke-103"),sQuery(id+"F0.wireOp",EDGE,"E15.sketch_text.stroke-104"),sQuery(id+"F0.wireOp",EDGE,"E15.sketch_text.stroke-105"),sQuery(id+"F0.wireOp",EDGE,"E15.sketch_text.stroke-106"),sQuery(id+"F0.wireOp",EDGE,"E15.sketch_text.stroke-107"),sQuery(id+"F0.wireOp",EDGE,"E15.sketch_text.stroke-108"),sQuery(id+"F0.wireOp",EDGE,"E15.sketch_text.stroke-109"),sQuery(id+"F0.wireOp",EDGE,"E15.sketch_text.stroke-110"),sQuery(id+"F0.wireOp",EDGE,"E15.sketch_text.stroke-111"),sQuery(id+"F0.wireOp",EDGE,"E15.sketch_text.stroke-112"),sQuery(id+"F0.wireOp",EDGE,"E15.sketch_text.stroke-113"),sQuery(id+"F0.wireOp",EDGE,"E15.sketch_text.stroke-114"),sQuery(id+"F0.wireOp",EDGE,"E15.sketch_text.stroke-115"),sQuery(id+"F0.wireOp",EDGE,"E15.sketch_text.stroke-116"),sQuery(id+"F0.wireOp",EDGE,"E15.sketch_text.stroke-117"),sQuery(id+"F0.wireOp",EDGE,"E15.sketch_text.stroke-118"),sQuery(id+"F0.wireOp",EDGE,"E15.sketch_text.stroke-119"),sQuery(id+"F0.wireOp",EDGE,"E15.sketch_text.stroke-120"),sQuery(id+"F0.wireOp",EDGE,"E15.sketch_text.stroke-121"),sQuery(id+"F0.wireOp",EDGE,"E15.sketch_text.stroke-122"),sQuery(id+"F0.wireOp",EDGE,"E15.sketch_text.stroke-123"),sQuery(id+"F0.wireOp",EDGE,"E15.sketch_text.stroke-124"),sQuery(id+"F0.wireOp",EDGE,"E15.sketch_text.stroke-125"),sQuery(id+"F0.wireOp",EDGE,"E15.sketch_text.stroke-126"),sQuery(id+"F0.wireOp",EDGE,"E15.sketch_text.stroke-127"),sQuery(id+"F0.wireOp",EDGE,"E15.sketch_text.stroke-128"),sQuery(id+"F0.wireOp",EDGE,"E15.sketch_text.stroke-129"),sQuery(id+"F0.wireOp",EDGE,"E15.sketch_text.stroke-130"),sQuery(id+"F0.wireOp",EDGE,"E15.sketch_text.stroke-131"),sQuery(id+"F0.wireOp",EDGE,"E15.sketch_text.stroke-132"),sQuery(id+"F0.wireOp",EDGE,"E15.sketch_text.stroke-133"),sQuery(id+"F0.wireOp",EDGE,"E15.sketch_text.stroke-134"),sQuery(id+"F0.wireOp",EDGE,"E15.sketch_text.stroke-135"),sQuery(id+"F0.wireOp",EDGE,"E15.sketch_text.stroke-136"),sQuery(id+"F0.wireOp",EDGE,"E15.sketch_text.stroke-137"),sQuery(id+"F0.wireOp",EDGE,"E15.sketch_text.stroke-138"),sQuery(id+"F0.wireOp",EDGE,"E15.sketch_text.stroke-139"),sQuery(id+"F0.wireOp",EDGE,"E15.sketch_text.stroke-140"),sQuery(id+"F0.wireOp",EDGE,"E15.sketch_text.stroke-141"),sQuery(id+"F0.wireOp",EDGE,"E15.sketch_text.stroke-142"),sQuery(id+"F0.wireOp",EDGE,"E15.sketch_text.stroke-143"),sQuery(id+"F0.wireOp",EDGE,"E15.sketch_text.stroke-144"),sQuery(id+"F0.wireOp",EDGE,"E15.sketch_text.stroke-145"),sQuery(id+"F0.wireOp",EDGE,"E15.sketch_text.stroke-146"),sQuery(id+"F0.wireOp",EDGE,"E15.sketch_text.stroke-147"),sQuery(id+"F0.wireOp",EDGE,"E15.sketch_text.stroke-148"),sQuery(id+"F0.wireOp",EDGE,"E15.sketch_text.stroke-149"),sQuery(id+"F0.wireOp",EDGE,"E15.sketch_text.stroke-150"),sQuery(id+"F0.wireOp",EDGE,"E15.sketch_text.stroke-151"),sQuery(id+"F0.wireOp",EDGE,"E15.sketch_text.stroke-152"),sQuery(id+"F0.wireOp",EDGE,"E15.sketch_text.stroke-153"),sQuery(id+"F0.wireOp",EDGE,"E15.sketch_text.stroke-154"),sQuery(id+"F0.wireOp",EDGE,"E15.sketch_text.stroke-155"),sQuery(id+"F0.wireOp",EDGE,"E15.sketch_text.stroke-156"),sQuery(id+"F0.wireOp",EDGE,"E15.sketch_text.stroke-157"),sQuery(id+"F0.wireOp",EDGE,"E15.sketch_text.stroke-158"),sQuery(id+"F0.wireOp",EDGE,"E15.sketch_text.stroke-159"),sQuery(id+"F0.wireOp",EDGE,"E15.sketch_text.stroke-160"),sQuery(id+"F0.wireOp",EDGE,"E15.sketch_text.stroke-161"),sQuery(id+"F0.wireOp",EDGE,"E16.bottom"),sQuery(id+"F0.wireOp",EDGE,"E17"),sQuery(id+"F0.wireOp",EDGE,"E19"),sQuery(id+"F0.wireOp",EDGE,"E21")])],"isStart":false})],"blendedInto":[makeQuery(id+"F1.opExtrude","CAP_FACE",FACE,{"disambiguationData":[OSD([sQuery(id+"F0.wireOp",EDGE,"E2"),subQ0,sQuery(id+"F0.wireOp",EDGE,"E4"),sQuery(id+"F0.wireOp",EDGE,"E5"),sQuery(id+"F0.wireOp",EDGE,"E6"),sQuery(id+"F0.wireOp",EDGE,"E7"),sQuery(id+"F0.wireOp",EDGE,"E8"),sQuery(id+"F0.wireOp",EDGE,"E9.sketch_text.stroke-0"),sQuery(id+"F0.wireOp",EDGE,"E9.sketch_text.stroke-1"),sQuery(id+"F0.wireOp",EDGE,"E9.sketch_text.stroke-2"),sQuery(id+"F0.wireOp",EDGE,"E9.sketch_text.stroke-3"),sQuery(id+"F0.wireOp",EDGE,"E9.sketch_text.stroke-4"),sQuery(id+"F0.wireOp",EDGE,"E9.sketch_text.stroke-5"),sQuery(id+"F0.wireOp",EDGE,"E9.sketch_text.stroke-6"),sQuery(id+"F0.wireOp",EDGE,"E9.sketch_text.stroke-7"),sQuery(id+"F0.wireOp",EDGE,"E9.sketch_text.stroke-8"),sQuery(id+"F0.wireOp",EDGE,"E9.sketch_text.stroke-9"),sQuery(id+"F0.wireOp",EDGE,"E9.sketch_text.stroke-10"),sQuery(id+"F0.wireOp",EDGE,"E9.sketch_text.stroke-11"),sQuery(id+"F0.wireOp",EDGE,"E9.sketch_text.stroke-12"),sQuery(id+"F0.wireOp",EDGE,"E9.sketch_text.stroke-13"),sQuery(id+"F0.wireOp",EDGE,"E9.sketch_text.stroke-14"),sQuery(id+"F0.wireOp",EDGE,"E9.sketch_text.stroke-15"),sQuery(id+"F0.wireOp",EDGE,"E9.sketch_text.stroke-16"),sQuery(id+"F0.wireOp",EDGE,"E9.sketch_text.stroke-17"),sQuery(id+"F0.wireOp",EDGE,"E9.sketch_text.stroke-18"),sQuery(id+"F0.wireOp",EDGE,"E9.sketch_text.stroke-27"),sQuery(id+"F0.wireOp",EDGE,"E9.sketch_text.stroke-28"),sQuery(id+"F0.wireOp",EDGE,"E9.sketch_text.stroke-29"),sQuery(id+"F0.wireOp",EDGE,"E9.sketch_text.stroke-30"),sQuery(id+"F0.wireOp",EDGE,"E9.sketch_text.stroke-31"),sQuery(id+"F0.wireOp",EDGE,"E9.sketch_text.stroke-32"),sQuery(id+"F0.wireOp",EDGE,"E9.sketch_text.stroke-33"),sQuery(id+"F0.wireOp",EDGE,"E9.sketch_text.stroke-34"),sQuery(id+"F0.wireOp",EDGE,"E9.sketch_text.stroke-35"),sQuery(id+"F0.wireOp",EDGE,"E9.sketch_text.stroke-36"),sQuery(id+"F0.wireOp",EDGE,"E9.sketch_text.stroke-37"),sQuery(id+"F0.wireOp",EDGE,"E9.sketch_text.stroke-38"),sQuery(id+"F0.wireOp",EDGE,"E9.sketch_text.stroke-39"),sQuery(id+"F0.wireOp",EDGE,"E9.sketch_text.stroke-40"),sQuery(id+"F0.wireOp",EDGE,"E9.sketch_text.stroke-41"),sQuery(id+"F0.wireOp",EDGE,"E9.sketch_text.stroke-42"),sQuery(id+"F0.wireOp",EDGE,"E9.sketch_text.stroke-43"),sQuery(id+"F0.wireOp",EDGE,"E9.sketch_text.stroke-44"),sQuery(id+"F0.wireOp",EDGE,"E9.sketch_text.stroke-45"),sQuery(id+"F0.wireOp",EDGE,"E9.sketch_text.stroke-46"),sQuery(id+"F0.wireOp",EDGE,"E9.sketch_text.stroke-47"),sQuery(id+"F0.wireOp",EDGE,"E9.sketch_text.stroke-48"),sQuery(id+"F0.wireOp",EDGE,"E9.sketch_text.stroke-49"),sQuery(id+"F0.wireOp",EDGE,"E9.sketch_text.stroke-50"),sQuery(id+"F0.wireOp",EDGE,"E9.sketch_text.stroke-51"),sQuery(id+"F0.wireOp",EDGE,"E9.sketch_text.stroke-52"),sQuery(id+"F0.wireOp",EDGE,"E9.sketch_text.stroke-53"),sQuery(id+"F0.wireOp",EDGE,"E9.sketch_text.stroke-54"),sQuery(id+"F0.wireOp",EDGE,"E9.sketch_text.stroke-55"),sQuery(id+"F0.wireOp",EDGE,"E9.sketch_text.stroke-56"),sQuery(id+"F0.wireOp",EDGE,"E9.sketch_text.stroke-57"),sQuery(id+"F0.wireOp",EDGE,"E9.sketch_text.stroke-58"),sQuery(id+"F0.wireOp",EDGE,"E9.sketch_text.stroke-59"),sQuery(id+"F0.wireOp",EDGE,"E9.sketch_text.stroke-60"),sQuery(id+"F0.wireOp",EDGE,"E9.sketch_text.stroke-61"),sQuery(id+"F0.wireOp",EDGE,"E9.sketch_text.stroke-62"),sQuery(id+"F0.wireOp",EDGE,"E9.sketch_text.stroke-63"),sQuery(id+"F0.wireOp",EDGE,"E9.sketch_text.stroke-64"),sQuery(id+"F0.wireOp",EDGE,"E9.sketch_text.stroke-65"),sQuery(id+"F0.wireOp",EDGE,"E9.sketch_text.stroke-66"),sQuery(id+"F0.wireOp",EDGE,"E9.sketch_text.stroke-67"),sQuery(id+"F0.wireOp",EDGE,"E9.sketch_text.stroke-68"),sQuery(id+"F0.wireOp",EDGE,"E9.sketch_text.stroke-69"),sQuery(id+"F0.wireOp",EDGE,"E9.sketch_text.stroke-70"),sQuery(id+"F0.wireOp",EDGE,"E9.sketch_text.stroke-71"),sQuery(id+"F0.wireOp",EDGE,"E9.sketch_text.stroke-72"),sQuery(id+"F0.wireOp",EDGE,"E9.sketch_text.stroke-73"),sQuery(id+"F0.wireOp",EDGE,"E9.sketch_text.stroke-74"),sQuery(id+"F0.wireOp",EDGE,"E9.sketch_text.stroke-75"),sQuery(id+"F0.wireOp",EDGE,"E9.sketch_text.stroke-76"),sQuery(id+"F0.wireOp",EDGE,"E9.sketch_text.stroke-77"),sQuery(id+"F0.wireOp",EDGE,"E9.sketch_text.stroke-78"),sQuery(id+"F0.wireOp",EDGE,"E9.sketch_text.stroke-79"),sQuery(id+"F0.wireOp",EDGE,"E9.sketch_text.stroke-80"),sQuery(id+"F0.wireOp",EDGE,"E9.sketch_text.stroke-81"),sQuery(id+"F0.wireOp",EDGE,"E9.sketch_text.stroke-82"),sQuery(id+"F0.wireOp",EDGE,"E9.sketch_text.stroke-83"),sQuery(id+"F0.wireOp",EDGE,"E9.sketch_text.stroke-84"),sQuery(id+"F0.wireOp",EDGE,"E9.sketch_text.stroke-85"),sQuery(id+"F0.wireOp",EDGE,"E9.sketch_text.stroke-86"),sQuery(id+"F0.wireOp",EDGE,"E9.sketch_text.stroke-87"),sQuery(id+"F0.wireOp",EDGE,"E9.sketch_text.stroke-88"),sQuery(id+"F0.wireOp",EDGE,"E9.sketch_text.stroke-89"),sQuery(id+"F0.wireOp",EDGE,"E9.sketch_text.stroke-90"),sQuery(id+"F0.wireOp",EDGE,"E9.sketch_text.stroke-91"),sQuery(id+"F0.wireOp",EDGE,"E9.sketch_text.stroke-92"),sQuery(id+"F0.wireOp",EDGE,"E9.sketch_text.stroke-93"),sQuery(id+"F0.wireOp",EDGE,"E9.sketch_text.stroke-94"),sQuery(id+"F0.wireOp",EDGE,"E9.sketch_text.stroke-95"),sQuery(id+"F0.wireOp",EDGE,"E9.sketch_text.stroke-96"),sQuery(id+"F0.wireOp",EDGE,"E9.sketch_text.stroke-97"),sQuery(id+"F0.wireOp",EDGE,"E9.sketch_text.stroke-98"),sQuery(id+"F0.wireOp",EDGE,"E9.sketch_text.stroke-99"),sQuery(id+"F0.wireOp",EDGE,"E9.sketch_text.stroke-100"),sQuery(id+"F0.wireOp",EDGE,"E9.sketch_text.stroke-101"),sQuery(id+"F0.wireOp",EDGE,"E9.sketch_text.stroke-102"),sQuery(id+"F0.wireOp",EDGE,"E9.sketch_text.stroke-103"),sQuery(id+"F0.wireOp",EDGE,"E9.sketch_text.stroke-104"),sQuery(id+"F0.wireOp",EDGE,"E9.sketch_text.stroke-105"),sQuery(id+"F0.wireOp",EDGE,"E9.sketch_text.stroke-106"),sQuery(id+"F0.wireOp",EDGE,"E9.sketch_text.stroke-107"),sQuery(id+"F0.wireOp",EDGE,"E9.sketch_text.stroke-108"),sQuery(id+"F0.wireOp",EDGE,"E9.sketch_text.stroke-109"),sQuery(id+"F0.wireOp",EDGE,"E9.sketch_text.stroke-110"),sQuery(id+"F0.wireOp",EDGE,"E9.sketch_text.stroke-111"),sQuery(id+"F0.wireOp",EDGE,"E9.sketch_text.stroke-112"),sQuery(id+"F0.wireOp",EDGE,"E9.sketch_text.stroke-113"),sQuery(id+"F0.wireOp",EDGE,"E9.sketch_text.stroke-114"),sQuery(id+"F0.wireOp",EDGE,"E9.sketch_text.stroke-115"),sQuery(id+"F0.wireOp",EDGE,"E9.sketch_text.stroke-116"),sQuery(id+"F0.wireOp",EDGE,"E9.sketch_text.stroke-117"),sQuery(id+"F0.wireOp",EDGE,"E9.sketch_text.stroke-118"),sQuery(id+"F0.wireOp",EDGE,"E9.sketch_text.stroke-119"),sQuery(id+"F0.wireOp",EDGE,"E9.sketch_text.stroke-120"),sQuery(id+"F0.wireOp",EDGE,"E9.sketch_text.stroke-126"),sQuery(id+"F0.wireOp",EDGE,"E9.sketch_text.stroke-127"),sQuery(id+"F0.wireOp",EDGE,"E9.sketch_text.stroke-128"),sQuery(id+"F0.wireOp",EDGE,"E9.sketch_text.stroke-129"),sQuery(id+"F0.wireOp",EDGE,"E9.sketch_text.stroke-130"),sQuery(id+"F0.wireOp",EDGE,"E9.sketch_text.stroke-131"),sQuery(id+"F0.wireOp",EDGE,"E9.sketch_text.stroke-132"),sQuery(id+"F0.wireOp",EDGE,"E9.sketch_text.stroke-133"),sQuery(id+"F0.wireOp",EDGE,"E9.sketch_text.stroke-134"),sQuery(id+"F0.wireOp",EDGE,"E9.sketch_text.stroke-135"),sQuery(id+"F0.wireOp",EDGE,"E9.sketch_text.stroke-136"),sQuery(id+"F0.wireOp",EDGE,"E9.sketch_text.stroke-137"),sQuery(id+"F0.wireOp",EDGE,"E9.sketch_text.stroke-138"),sQuery(id+"F0.wireOp",EDGE,"E9.sketch_text.stroke-139"),sQuery(id+"F0.wireOp",EDGE,"E9.sketch_text.stroke-140"),sQuery(id+"F0.wireOp",EDGE,"E9.sketch_text.stroke-141"),sQuery(id+"F0.wireOp",EDGE,"E9.sketch_text.stroke-142"),sQuery(id+"F0.wireOp",EDGE,"E9.sketch_text.stroke-143"),sQuery(id+"F0.wireOp",EDGE,"E9.sketch_text.stroke-144"),sQuery(id+"F0.wireOp",EDGE,"E9.sketch_text.stroke-145"),sQuery(id+"F0.wireOp",EDGE,"E9.sketch_text.stroke-146"),sQuery(id+"F0.wireOp",EDGE,"E9.sketch_text.stroke-147"),sQuery(id+"F0.wireOp",EDGE,"E9.sketch_text.stroke-148"),sQuery(id+"F0.wireOp",EDGE,"E9.sketch_text.stroke-149"),sQuery(id+"F0.wireOp",EDGE,"E9.sketch_text.stroke-150"),sQuery(id+"F0.wireOp",EDGE,"E9.sketch_text.stroke-151"),sQuery(id+"F0.wireOp",EDGE,"E9.sketch_text.stroke-152"),sQuery(id+"F0.wireOp",EDGE,"E9.sketch_text.stroke-153"),sQuery(id+"F0.wireOp",EDGE,"E9.sketch_text.stroke-154"),sQuery(id+"F0.wireOp",EDGE,"E9.sketch_text.stroke-155"),sQuery(id+"F0.wireOp",EDGE,"E9.sketch_text.stroke-156"),sQuery(id+"F0.wireOp",EDGE,"E9.sketch_text.stroke-157"),sQuery(id+"F0.wireOp",EDGE,"E9.sketch_text.stroke-158"),sQuery(id+"F0.wireOp",EDGE,"E9.sketch_text.stroke-159"),sQuery(id+"F0.wireOp",EDGE,"E9.sketch_text.stroke-160"),sQuery(id+"F0.wireOp",EDGE,"E9.sketch_text.stroke-161"),sQuery(id+"F0.wireOp",EDGE,"E9.sketch_text.stroke-162"),sQuery(id+"F0.wireOp",EDGE,"E9.sketch_text.stroke-163"),sQuery(id+"F0.wireOp",EDGE,"E9.sketch_text.stroke-164"),sQuery(id+"F0.wireOp",EDGE,"E9.sketch_text.stroke-165"),sQuery(id+"F0.wireOp",EDGE,"E9.sketch_text.stroke-166"),sQuery(id+"F0.wireOp",EDGE,"E9.sketch_text.stroke-167"),sQuery(id+"F0.wireOp",EDGE,"E9.sketch_text.stroke-168"),sQuery(id+"F0.wireOp",EDGE,"E9.sketch_text.stroke-169"),sQuery(id+"F0.wireOp",EDGE,"E9.sketch_text.stroke-170"),sQuery(id+"F0.wireOp",EDGE,"E9.sketch_text.stroke-171"),sQuery(id+"F0.wireOp",EDGE,"E9.sketch_text.stroke-172"),sQuery(id+"F0.wireOp",EDGE,"E9.sketch_text.stroke-173"),sQuery(id+"F0.wireOp",EDGE,"E11.top"),sQuery(id+"F0.wireOp",EDGE,"E12.sketch_text.stroke-0"),sQuery(id+"F0.wireOp",EDGE,"E12.sketch_text.stroke-1"),sQuery(id+"F0.wireOp",EDGE,"E12.sketch_text.stroke-2"),sQuery(id+"F0.wireOp",EDGE,"E12.sketch_text.stroke-3"),sQuery(id+"F0.wireOp",EDGE,"E12.sketch_text.stroke-4"),sQuery(id+"F0.wireOp",EDGE,"E12.sketch_text.stroke-5"),sQuery(id+"F0.wireOp",EDGE,"E12.sketch_text.stroke-6"),sQuery(id+"F0.wireOp",EDGE,"E12.sketch_text.stroke-7"),sQuery(id+"F0.wireOp",EDGE,"E12.sketch_text.stroke-8"),sQuery(id+"F0.wireOp",EDGE,"E12.sketch_text.stroke-9"),sQuery(id+"F0.wireOp",EDGE,"E12.sketch_text.stroke-10"),sQuery(id+"F0.wireOp",EDGE,"E12.sketch_text.stroke-11"),sQuery(id+"F0.wireOp",EDGE,"E12.sketch_text.stroke-12"),sQuery(id+"F0.wireOp",EDGE,"E12.sketch_text.stroke-13"),sQuery(id+"F0.wireOp",EDGE,"E12.sketch_text.stroke-14"),sQuery(id+"F0.wireOp",EDGE,"E12.sketch_text.stroke-15"),sQuery(id+"F0.wireOp",EDGE,"E12.sketch_text.stroke-16"),sQuery(id+"F0.wireOp",EDGE,"E12.sketch_text.stroke-17"),sQuery(id+"F0.wireOp",EDGE,"E12.sketch_text.stroke-18"),sQuery(id+"F0.wireOp",EDGE,"E12.sketch_text.stroke-19"),sQuery(id+"F0.wireOp",EDGE,"E12.sketch_text.stroke-20"),sQuery(id+"F0.wireOp",EDGE,"E12.sketch_text.stroke-21"),sQuery(id+"F0.wireOp",EDGE,"E12.sketch_text.stroke-22"),sQuery(id+"F0.wireOp",EDGE,"E12.sketch_text.stroke-23"),sQuery(id+"F0.wireOp",EDGE,"E12.sketch_text.stroke-24"),sQuery(id+"F0.wireOp",EDGE,"E12.sketch_text.stroke-25"),sQuery(id+"F0.wireOp",EDGE,"E12.sketch_text.stroke-26"),sQuery(id+"F0.wireOp",EDGE,"E12.sketch_text.stroke-27"),sQuery(id+"F0.wireOp",EDGE,"E12.sketch_text.stroke-28"),sQuery(id+"F0.wireOp",EDGE,"E12.sketch_text.stroke-29"),sQuery(id+"F0.wireOp",EDGE,"E12.sketch_text.stroke-30"),sQuery(id+"F0.wireOp",EDGE,"E12.sketch_text.stroke-31"),sQuery(id+"F0.wireOp",EDGE,"E12.sketch_text.stroke-32"),sQuery(id+"F0.wireOp",EDGE,"E12.sketch_text.stroke-33"),sQuery(id+"F0.wireOp",EDGE,"E12.sketch_text.stroke-34"),sQuery(id+"F0.wireOp",EDGE,"E13.sketch_text.stroke-0"),sQuery(id+"F0.wireOp",EDGE,"E13.sketch_text.stroke-1"),sQuery(id+"F0.wireOp",EDGE,"E13.sketch_text.stroke-2"),sQuery(id+"F0.wireOp",EDGE,"E13.sketch_text.stroke-3"),sQuery(id+"F0.wireOp",EDGE,"E13.sketch_text.stroke-4"),sQuery(id+"F0.wireOp",EDGE,"E13.sketch_text.stroke-5"),sQuery(id+"F0.wireOp",EDGE,"E13.sketch_text.stroke-6"),sQuery(id+"F0.wireOp",EDGE,"E13.sketch_text.stroke-7"),sQuery(id+"F0.wireOp",EDGE,"E13.sketch_text.stroke-15"),sQuery(id+"F0.wireOp",EDGE,"E13.sketch_text.stroke-16"),sQuery(id+"F0.wireOp",EDGE,"E13.sketch_text.stroke-17"),sQuery(id+"F0.wireOp",EDGE,"E13.sketch_text.stroke-18"),sQuery(id+"F0.wireOp",EDGE,"E13.sketch_text.stroke-19"),sQuery(id+"F0.wireOp",EDGE,"E13.sketch_text.stroke-20"),sQuery(id+"F0.wireOp",EDGE,"E13.sketch_text.stroke-21"),sQuery(id+"F0.wireOp",EDGE,"E13.sketch_text.stroke-22"),sQuery(id+"F0.wireOp",EDGE,"E13.sketch_text.stroke-23"),sQuery(id+"F0.wireOp",EDGE,"E13.sketch_text.stroke-24"),sQuery(id+"F0.wireOp",EDGE,"E13.sketch_text.stroke-25"),sQuery(id+"F0.wireOp",EDGE,"E13.sketch_text.stroke-26"),sQuery(id+"F0.wireOp",EDGE,"E13.sketch_text.stroke-27"),sQuery(id+"F0.wireOp",EDGE,"E13.sketch_text.stroke-28"),sQuery(id+"F0.wireOp",EDGE,"E13.sketch_text.stroke-29"),sQuery(id+"F0.wireOp",EDGE,"E13.sketch_text.stroke-30"),sQuery(id+"F0.wireOp",EDGE,"E13.sketch_text.stroke-31"),sQuery(id+"F0.wireOp",EDGE,"E13.sketch_text.stroke-32"),sQuery(id+"F0.wireOp",EDGE,"E13.sketch_text.stroke-33"),sQuery(id+"F0.wireOp",EDGE,"E13.sketch_text.stroke-34"),sQuery(id+"F0.wireOp",EDGE,"E13.sketch_text.stroke-35"),sQuery(id+"F0.wireOp",EDGE,"E13.sketch_text.stroke-36"),sQuery(id+"F0.wireOp",EDGE,"E13.sketch_text.stroke-45"),sQuery(id+"F0.wireOp",EDGE,"E13.sketch_text.stroke-46"),sQuery(id+"F0.wireOp",EDGE,"E13.sketch_text.stroke-47"),sQuery(id+"F0.wireOp",EDGE,"E13.sketch_text.stroke-48"),sQuery(id+"F0.wireOp",EDGE,"E13.sketch_text.stroke-49"),sQuery(id+"F0.wireOp",EDGE,"E13.sketch_text.stroke-50"),sQuery(id+"F0.wireOp",EDGE,"E13.sketch_text.stroke-51"),sQuery(id+"F0.wireOp",EDGE,"E13.sketch_text.stroke-52"),sQuery(id+"F0.wireOp",EDGE,"E13.sketch_text.stroke-53"),sQuery(id+"F0.wireOp",EDGE,"E13.sketch_text.stroke-54"),sQuery(id+"F0.wireOp",EDGE,"E13.sketch_text.stroke-55"),sQuery(id+"F0.wireOp",EDGE,"E13.sketch_text.stroke-56"),sQuery(id+"F0.wireOp",EDGE,"E13.sketch_text.stroke-57"),sQuery(id+"F0.wireOp",EDGE,"E13.sketch_text.stroke-58"),sQuery(id+"F0.wireOp",EDGE,"E13.sketch_text.stroke-59"),sQuery(id+"F0.wireOp",EDGE,"E13.sketch_text.stroke-69"),sQuery(id+"F0.wireOp",EDGE,"E13.sketch_text.stroke-70"),sQuery(id+"F0.wireOp",EDGE,"E13.sketch_text.stroke-71"),sQuery(id+"F0.wireOp",EDGE,"E13.sketch_text.stroke-72"),sQuery(id+"F0.wireOp",EDGE,"E13.sketch_text.stroke-73"),sQuery(id+"F0.wireOp",EDGE,"E13.sketch_text.stroke-74"),sQuery(id+"F0.wireOp",EDGE,"E13.sketch_text.stroke-75"),sQuery(id+"F0.wireOp",EDGE,"E13.sketch_text.stroke-76"),sQuery(id+"F0.wireOp",EDGE,"E13.sketch_text.stroke-77"),sQuery(id+"F0.wireOp",EDGE,"E13.sketch_text.stroke-78"),sQuery(id+"F0.wireOp",EDGE,"E13.sketch_text.stroke-79"),sQuery(id+"F0.wireOp",EDGE,"E13.sketch_text.stroke-80"),sQuery(id+"F0.wireOp",EDGE,"E13.sketch_text.stroke-81"),sQuery(id+"F0.wireOp",EDGE,"E13.sketch_text.stroke-82"),sQuery(id+"F0.wireOp",EDGE,"E13.sketch_text.stroke-83"),sQuery(id+"F0.wireOp",EDGE,"E13.sketch_text.stroke-84"),sQuery(id+"F0.wireOp",EDGE,"E13.sketch_text.stroke-85"),sQuery(id+"F0.wireOp",EDGE,"E13.sketch_text.stroke-86"),sQuery(id+"F0.wireOp",EDGE,"E13.sketch_text.stroke-87"),sQuery(id+"F0.wireOp",EDGE,"E13.sketch_text.stroke-88"),sQuery(id+"F0.wireOp",EDGE,"E13.sketch_text.stroke-89"),sQuery(id+"F0.wireOp",EDGE,"E13.sketch_text.stroke-90"),sQuery(id+"F0.wireOp",EDGE,"E13.sketch_text.stroke-91"),sQuery(id+"F0.wireOp",EDGE,"E13.sketch_text.stroke-92"),sQuery(id+"F0.wireOp",EDGE,"E13.sketch_text.stroke-93"),sQuery(id+"F0.wireOp",EDGE,"E13.sketch_text.stroke-94"),sQuery(id+"F0.wireOp",EDGE,"E13.sketch_text.stroke-95"),sQuery(id+"F0.wireOp",EDGE,"E13.sketch_text.stroke-96"),sQuery(id+"F0.wireOp",EDGE,"E13.sketch_text.stroke-97"),sQuery(id+"F0.wireOp",EDGE,"E13.sketch_text.stroke-98"),sQuery(id+"F0.wireOp",EDGE,"E13.sketch_text.stroke-99"),sQuery(id+"F0.wireOp",EDGE,"E13.sketch_text.stroke-100"),sQuery(id+"F0.wireOp",EDGE,"E13.sketch_text.stroke-101"),sQuery(id+"F0.wireOp",EDGE,"E13.sketch_text.stroke-102"),sQuery(id+"F0.wireOp",EDGE,"E13.sketch_text.stroke-103"),sQuery(id+"F0.wireOp",EDGE,"E13.sketch_text.stroke-104"),sQuery(id+"F0.wireOp",EDGE,"E13.sketch_text.stroke-105"),sQuery(id+"F0.wireOp",EDGE,"E13.sketch_text.stroke-106"),sQuery(id+"F0.wireOp",EDGE,"E13.sketch_text.stroke-107"),sQuery(id+"F0.wireOp",EDGE,"E13.sketch_text.stroke-108"),sQuery(id+"F0.wireOp",EDGE,"E13.sketch_text.stroke-109"),sQuery(id+"F0.wireOp",EDGE,"E13.sketch_text.stroke-110"),sQuery(id+"F0.wireOp",EDGE,"E13.sketch_text.stroke-111"),sQuery(id+"F0.wireOp",EDGE,"E13.sketch_text.stroke-112"),sQuery(id+"F0.wireOp",EDGE,"E13.sketch_text.stroke-113"),sQuery(id+"F0.wireOp",EDGE,"E13.sketch_text.stroke-114"),sQuery(id+"F0.wireOp",EDGE,"E13.sketch_text.stroke-115"),sQuery(id+"F0.wireOp",EDGE,"E13.sketch_text.stroke-116"),sQuery(id+"F0.wireOp",EDGE,"E13.sketch_text.stroke-117"),sQuery(id+"F0.wireOp",EDGE,"E13.sketch_text.stroke-118"),sQuery(id+"F0.wireOp",EDGE,"E13.sketch_text.stroke-119"),sQuery(id+"F0.wireOp",EDGE,"E13.sketch_text.stroke-120"),sQuery(id+"F0.wireOp",EDGE,"E13.sketch_text.stroke-121"),sQuery(id+"F0.wireOp",EDGE,"E13.sketch_text.stroke-122"),sQuery(id+"F0.wireOp",EDGE,"E13.sketch_text.stroke-123"),sQuery(id+"F0.wireOp",EDGE,"E13.sketch_text.stroke-124"),sQuery(id+"F0.wireOp",EDGE,"E13.sketch_text.stroke-125"),sQuery(id+"F0.wireOp",EDGE,"E13.sketch_text.stroke-126"),sQuery(id+"F0.wireOp",EDGE,"E13.sketch_text.stroke-127"),sQuery(id+"F0.wireOp",EDGE,"E13.sketch_text.stroke-128"),sQuery(id+"F0.wireOp",EDGE,"E13.sketch_text.stroke-129"),sQuery(id+"F0.wireOp",EDGE,"E13.sketch_text.stroke-130"),sQuery(id+"F0.wireOp",EDGE,"E13.sketch_text.stroke-131"),sQuery(id+"F0.wireOp",EDGE,"E13.sketch_text.stroke-132"),sQuery(id+"F0.wireOp",EDGE,"E13.sketch_text.stroke-133"),sQuery(id+"F0.wireOp",EDGE,"E13.sketch_text.stroke-134"),sQuery(id+"F0.wireOp",EDGE,"E13.sketch_text.stroke-135"),sQuery(id+"F0.wireOp",EDGE,"E13.sketch_text.stroke-136"),sQuery(id+"F0.wireOp",EDGE,"E13.sketch_text.stroke-137"),sQuery(id+"F0.wireOp",EDGE,"E13.sketch_text.stroke-138"),sQuery(id+"F0.wireOp",EDGE,"E13.sketch_text.stroke-139"),sQuery(id+"F0.wireOp",EDGE,"E13.sketch_text.stroke-140"),sQuery(id+"F0.wireOp",EDGE,"E13.sketch_text.stroke-149"),sQuery(id+"F0.wireOp",EDGE,"E13.sketch_text.stroke-150"),sQuery(id+"F0.wireOp",EDGE,"E13.sketch_text.stroke-151"),sQuery(id+"F0.wireOp",EDGE,"E13.sketch_text.stroke-152"),sQuery(id+"F0.wireOp",EDGE,"E13.sketch_text.stroke-153"),sQuery(id+"F0.wireOp",EDGE,"E13.sketch_text.stroke-154"),sQuery(id+"F0.wireOp",EDGE,"E13.sketch_text.stroke-155"),sQuery(id+"F0.wireOp",EDGE,"E13.sketch_text.stroke-156"),sQuery(id+"F0.wireOp",EDGE,"E13.sketch_text.stroke-157"),sQuery(id+"F0.wireOp",EDGE,"E13.sketch_text.stroke-158"),sQuery(id+"F0.wireOp",EDGE,"E13.sketch_text.stroke-159"),sQuery(id+"F0.wireOp",EDGE,"E13.sketch_text.stroke-160"),sQuery(id+"F0.wireOp",EDGE,"E13.sketch_text.stroke-161"),sQuery(id+"F0.wireOp",EDGE,"E13.sketch_text.stroke-162"),sQuery(id+"F0.wireOp",EDGE,"E13.sketch_text.stroke-163"),sQuery(id+"F0.wireOp",EDGE,"E13.sketch_text.stroke-164"),sQuery(id+"F0.wireOp",EDGE,"E13.sketch_text.stroke-165"),sQuery(id+"F0.wireOp",EDGE,"E13.sketch_text.stroke-166"),sQuery(id+"F0.wireOp",EDGE,"E13.sketch_text.stroke-167"),sQuery(id+"F0.wireOp",EDGE,"E13.sketch_text.stroke-168"),sQuery(id+"F0.wireOp",EDGE,"E13.sketch_text.stroke-169"),sQuery(id+"F0.wireOp",EDGE,"E13.sketch_text.stroke-170"),sQuery(id+"F0.wireOp",EDGE,"E13.sketch_text.stroke-171"),sQuery(id+"F0.wireOp",EDGE,"E13.sketch_text.stroke-172"),sQuery(id+"F0.wireOp",EDGE,"E13.sketch_text.stroke-173"),sQuery(id+"F0.wireOp",EDGE,"E13.sketch_text.stroke-174"),sQuery(id+"F0.wireOp",EDGE,"E13.sketch_text.stroke-175"),sQuery(id+"F0.wireOp",EDGE,"E13.sketch_text.stroke-176"),sQuery(id+"F0.wireOp",EDGE,"E13.sketch_text.stroke-177"),sQuery(id+"F0.wireOp",EDGE,"E13.sketch_text.stroke-178"),sQuery(id+"F0.wireOp",EDGE,"E13.sketch_text.stroke-179"),sQuery(id+"F0.wireOp",EDGE,"E13.sketch_text.stroke-180"),sQuery(id+"F0.wireOp",EDGE,"E13.sketch_text.stroke-181"),sQuery(id+"F0.wireOp",EDGE,"E13.sketch_text.stroke-182"),sQuery(id+"F0.wireOp",EDGE,"E13.sketch_text.stroke-183"),sQuery(id+"F0.wireOp",EDGE,"E13.sketch_text.stroke-184"),sQuery(id+"F0.wireOp",EDGE,"E13.sketch_text.stroke-185"),sQuery(id+"F0.wireOp",EDGE,"E13.sketch_text.stroke-186"),sQuery(id+"F0.wireOp",EDGE,"E13.sketch_text.stroke-187"),sQuery(id+"F0.wireOp",EDGE,"E13.sketch_text.stroke-188"),sQuery(id+"F0.wireOp",EDGE,"E13.sketch_text.stroke-189"),sQuery(id+"F0.wireOp",EDGE,"E13.sketch_text.stroke-190"),sQuery(id+"F0.wireOp",EDGE,"E14.sketch_text.stroke-0"),sQuery(id+"F0.wireOp",EDGE,"E14.sketch_text.stroke-1"),sQuery(id+"F0.wireOp",EDGE,"E14.sketch_text.stroke-2"),sQuery(id+"F0.wireOp",EDGE,"E14.sketch_text.stroke-3"),sQuery(id+"F0.wireOp",EDGE,"E14.sketch_text.stroke-4"),sQuery(id+"F0.wireOp",EDGE,"E14.sketch_text.stroke-5"),sQuery(id+"F0.wireOp",EDGE,"E14.sketch_text.stroke-6"),sQuery(id+"F0.wireOp",EDGE,"E14.sketch_text.stroke-7"),sQuery(id+"F0.wireOp",EDGE,"E14.sketch_text.stroke-8"),sQuery(id+"F0.wireOp",EDGE,"E14.sketch_text.stroke-9"),sQuery(id+"F0.wireOp",EDGE,"E14.sketch_text.stroke-10"),sQuery(id+"F0.wireOp",EDGE,"E14.sketch_text.stroke-11"),sQuery(id+"F0.wireOp",EDGE,"E14.sketch_text.stroke-12"),sQuery(id+"F0.wireOp",EDGE,"E14.sketch_text.stroke-13"),sQuery(id+"F0.wireOp",EDGE,"E14.sketch_text.stroke-14"),sQuery(id+"F0.wireOp",EDGE,"E14.sketch_text.stroke-15"),sQuery(id+"F0.wireOp",EDGE,"E14.sketch_text.stroke-25"),sQuery(id+"F0.wireOp",EDGE,"E14.sketch_text.stroke-26"),sQuery(id+"F0.wireOp",EDGE,"E14.sketch_text.stroke-27"),sQuery(id+"F0.wireOp",EDGE,"E14.sketch_text.stroke-28"),sQuery(id+"F0.wireOp",EDGE,"E14.sketch_text.stroke-29"),sQuery(id+"F0.wireOp",EDGE,"E14.sketch_text.stroke-30"),sQuery(id+"F0.wireOp",EDGE,"E14.sketch_text.stroke-31"),sQuery(id+"F0.wireOp",EDGE,"E14.sketch_text.stroke-32"),sQuery(id+"F0.wireOp",EDGE,"E14.sketch_text.stroke-33"),sQuery(id+"F0.wireOp",EDGE,"E14.sketch_text.stroke-34"),sQuery(id+"F0.wireOp",EDGE,"E14.sketch_text.stroke-35"),sQuery(id+"F0.wireOp",EDGE,"E14.sketch_text.stroke-36"),sQuery(id+"F0.wireOp",EDGE,"E14.sketch_text.stroke-37"),sQuery(id+"F0.wireOp",EDGE,"E14.sketch_text.stroke-38"),sQuery(id+"F0.wireOp",EDGE,"E14.sketch_text.stroke-39"),sQuery(id+"F0.wireOp",EDGE,"E14.sketch_text.stroke-40"),sQuery(id+"F0.wireOp",EDGE,"E14.sketch_text.stroke-41"),sQuery(id+"F0.wireOp",EDGE,"E14.sketch_text.stroke-42"),sQuery(id+"F0.wireOp",EDGE,"E14.sketch_text.stroke-43"),sQuery(id+"F0.wireOp",EDGE,"E14.sketch_text.stroke-44"),sQuery(id+"F0.wireOp",EDGE,"E14.sketch_text.stroke-45"),sQuery(id+"F0.wireOp",EDGE,"E14.sketch_text.stroke-46"),sQuery(id+"F0.wireOp",EDGE,"E14.sketch_text.stroke-55"),sQuery(id+"F0.wireOp",EDGE,"E14.sketch_text.stroke-56"),sQuery(id+"F0.wireOp",EDGE,"E14.sketch_text.stroke-57"),sQuery(id+"F0.wireOp",EDGE,"E14.sketch_text.stroke-58"),sQuery(id+"F0.wireOp",EDGE,"E14.sketch_text.stroke-59"),sQuery(id+"F0.wireOp",EDGE,"E14.sketch_text.stroke-60"),sQuery(id+"F0.wireOp",EDGE,"E14.sketch_text.stroke-61"),sQuery(id+"F0.wireOp",EDGE,"E14.sketch_text.stroke-62"),sQuery(id+"F0.wireOp",EDGE,"E14.sketch_text.stroke-63"),sQuery(id+"F0.wireOp",EDGE,"E14.sketch_text.stroke-64"),sQuery(id+"F0.wireOp",EDGE,"E14.sketch_text.stroke-65"),sQuery(id+"F0.wireOp",EDGE,"E14.sketch_text.stroke-66"),sQuery(id+"F0.wireOp",EDGE,"E14.sketch_text.stroke-67"),sQuery(id+"F0.wireOp",EDGE,"E14.sketch_text.stroke-68"),sQuery(id+"F0.wireOp",EDGE,"E14.sketch_text.stroke-69"),sQuery(id+"F0.wireOp",EDGE,"E14.sketch_text.stroke-70"),sQuery(id+"F0.wireOp",EDGE,"E14.sketch_text.stroke-71"),sQuery(id+"F0.wireOp",EDGE,"E14.sketch_text.stroke-72"),sQuery(id+"F0.wireOp",EDGE,"E14.sketch_text.stroke-73"),sQuery(id+"F0.wireOp",EDGE,"E14.sketch_text.stroke-74"),sQuery(id+"F0.wireOp",EDGE,"E14.sketch_text.stroke-75"),sQuery(id+"F0.wireOp",EDGE,"E14.sketch_text.stroke-76"),sQuery(id+"F0.wireOp",EDGE,"E14.sketch_text.stroke-77"),sQuery(id+"F0.wireOp",EDGE,"E14.sketch_text.stroke-78"),sQuery(id+"F0.wireOp",EDGE,"E14.sketch_text.stroke-79"),sQuery(id+"F0.wireOp",EDGE,"E14.sketch_text.stroke-80"),sQuery(id+"F0.wireOp",EDGE,"E14.sketch_text.stroke-81"),sQuery(id+"F0.wireOp",EDGE,"E14.sketch_text.stroke-82"),sQuery(id+"F0.wireOp",EDGE,"E14.sketch_text.stroke-83"),sQuery(id+"F0.wireOp",EDGE,"E14.sketch_text.stroke-84"),sQuery(id+"F0.wireOp",EDGE,"E14.sketch_text.stroke-85"),sQuery(id+"F0.wireOp",EDGE,"E14.sketch_text.stroke-86"),sQuery(id+"F0.wireOp",EDGE,"E14.sketch_text.stroke-96"),sQuery(id+"F0.wireOp",EDGE,"E14.sketch_text.stroke-97"),sQuery(id+"F0.wireOp",EDGE,"E14.sketch_text.stroke-98"),sQuery(id+"F0.wireOp",EDGE,"E14.sketch_text.stroke-99"),sQuery(id+"F0.wireOp",EDGE,"E14.sketch_text.stroke-100"),sQuery(id+"F0.wireOp",EDGE,"E14.sketch_text.stroke-101"),sQuery(id+"F0.wireOp",EDGE,"E14.sketch_text.stroke-102"),sQuery(id+"F0.wireOp",EDGE,"E14.sketch_text.stroke-103"),sQuery(id+"F0.wireOp",EDGE,"E14.sketch_text.stroke-104"),sQuery(id+"F0.wireOp",EDGE,"E14.sketch_text.stroke-105"),sQuery(id+"F0.wireOp",EDGE,"E14.sketch_text.stroke-106"),sQuery(id+"F0.wireOp",EDGE,"E14.sketch_text.stroke-107"),sQuery(id+"F0.wireOp",EDGE,"E14.sketch_text.stroke-108"),sQuery(id+"F0.wireOp",EDGE,"E14.sketch_text.stroke-109"),sQuery(id+"F0.wireOp",EDGE,"E14.sketch_text.stroke-110"),sQuery(id+"F0.wireOp",EDGE,"E14.sketch_text.stroke-111"),sQuery(id+"F0.wireOp",EDGE,"E14.sketch_text.stroke-112"),sQuery(id+"F0.wireOp",EDGE,"E14.sketch_text.stroke-113"),sQuery(id+"F0.wireOp",EDGE,"E14.sketch_text.stroke-114"),sQuery(id+"F0.wireOp",EDGE,"E14.sketch_text.stroke-115"),sQuery(id+"F0.wireOp",EDGE,"E15.sketch_text.stroke-0"),sQuery(id+"F0.wireOp",EDGE,"E15.sketch_text.stroke-1"),sQuery(id+"F0.wireOp",EDGE,"E15.sketch_text.stroke-2"),sQuery(id+"F0.wireOp",EDGE,"E15.sketch_text.stroke-3"),sQuery(id+"F0.wireOp",EDGE,"E15.sketch_text.stroke-4"),sQuery(id+"F0.wireOp",EDGE,"E15.sketch_text.stroke-5"),sQuery(id+"F0.wireOp",EDGE,"E15.sketch_text.stroke-6"),sQuery(id+"F0.wireOp",EDGE,"E15.sketch_text.stroke-7"),sQuery(id+"F0.wireOp",EDGE,"E15.sketch_text.stroke-8"),sQuery(id+"F0.wireOp",EDGE,"E15.sketch_text.stroke-9"),sQuery(id+"F0.wireOp",EDGE,"E15.sketch_text.stroke-10"),sQuery(id+"F0.wireOp",EDGE,"E15.sketch_text.stroke-11"),sQuery(id+"F0.wireOp",EDGE,"E15.sketch_text.stroke-12"),sQuery(id+"F0.wireOp",EDGE,"E15.sketch_text.stroke-13"),sQuery(id+"F0.wireOp",EDGE,"E15.sketch_text.stroke-14"),sQuery(id+"F0.wireOp",EDGE,"E15.sketch_text.stroke-15"),sQuery(id+"F0.wireOp",EDGE,"E15.sketch_text.stroke-25"),sQuery(id+"F0.wireOp",EDGE,"E15.sketch_text.stroke-26"),sQuery(id+"F0.wireOp",EDGE,"E15.sketch_text.stroke-27"),sQuery(id+"F0.wireOp",EDGE,"E15.sketch_text.stroke-28"),sQuery(id+"F0.wireOp",EDGE,"E15.sketch_text.stroke-29"),sQuery(id+"F0.wireOp",EDGE,"E15.sketch_text.stroke-30"),sQuery(id+"F0.wireOp",EDGE,"E15.sketch_text.stroke-31"),sQuery(id+"F0.wireOp",EDGE,"E15.sketch_text.stroke-32"),sQuery(id+"F0.wireOp",EDGE,"E15.sketch_text.stroke-33"),sQuery(id+"F0.wireOp",EDGE,"E15.sketch_text.stroke-34"),sQuery(id+"F0.wireOp",EDGE,"E15.sketch_text.stroke-35"),sQuery(id+"F0.wireOp",EDGE,"E15.sketch_text.stroke-36"),sQuery(id+"F0.wireOp",EDGE,"E15.sketch_text.stroke-37"),sQuery(id+"F0.wireOp",EDGE,"E15.sketch_text.stroke-38"),sQuery(id+"F0.wireOp",EDGE,"E15.sketch_text.stroke-39"),sQuery(id+"F0.wireOp",EDGE,"E15.sketch_text.stroke-40"),sQuery(id+"F0.wireOp",EDGE,"E15.sketch_text.stroke-41"),sQuery(id+"F0.wireOp",EDGE,"E15.sketch_text.stroke-42"),sQuery(id+"F0.wireOp",EDGE,"E15.sketch_text.stroke-43"),sQuery(id+"F0.wireOp",EDGE,"E15.sketch_text.stroke-44"),sQuery(id+"F0.wireOp",EDGE,"E15.sketch_text.stroke-45"),sQuery(id+"F0.wireOp",EDGE,"E15.sketch_text.stroke-46"),sQuery(id+"F0.wireOp",EDGE,"E15.sketch_text.stroke-47"),sQuery(id+"F0.wireOp",EDGE,"E15.sketch_text.stroke-48"),sQuery(id+"F0.wireOp",EDGE,"E15.sketch_text.stroke-49"),sQuery(id+"F0.wireOp",EDGE,"E15.sketch_text.stroke-50"),sQuery(id+"F0.wireOp",EDGE,"E15.sketch_text.stroke-51"),sQuery(id+"F0.wireOp",EDGE,"E15.sketch_text.stroke-57"),sQuery(id+"F0.wireOp",EDGE,"E15.sketch_text.stroke-58"),sQuery(id+"F0.wireOp",EDGE,"E15.sketch_text.stroke-59"),sQuery(id+"F0.wireOp",EDGE,"E15.sketch_text.stroke-60"),sQuery(id+"F0.wireOp",EDGE,"E15.sketch_text.stroke-61"),sQuery(id+"F0.wireOp",EDGE,"E15.sketch_text.stroke-62"),sQuery(id+"F0.wireOp",EDGE,"E15.sketch_text.stroke-63"),sQuery(id+"F0.wireOp",EDGE,"E15.sketch_text.stroke-64"),sQuery(id+"F0.wireOp",EDGE,"E15.sketch_text.stroke-65"),sQuery(id+"F0.wireOp",EDGE,"E15.sketch_text.stroke-66"),sQuery(id+"F0.wireOp",EDGE,"E15.sketch_text.stroke-67"),sQuery(id+"F0.wireOp",EDGE,"E15.sketch_text.stroke-68"),sQuery(id+"F0.wireOp",EDGE,"E15.sketch_text.stroke-69"),sQuery(id+"F0.wireOp",EDGE,"E15.sketch_text.stroke-70"),sQuery(id+"F0.wireOp",EDGE,"E15.sketch_text.stroke-71"),sQuery(id+"F0.wireOp",EDGE,"E15.sketch_text.stroke-72"),sQuery(id+"F0.wireOp",EDGE,"E15.sketch_text.stroke-73"),sQuery(id+"F0.wireOp",EDGE,"E15.sketch_text.stroke-74"),sQuery(id+"F0.wireOp",EDGE,"E15.sketch_text.stroke-75"),sQuery(id+"F0.wireOp",EDGE,"E15.sketch_text.stroke-76"),sQuery(id+"F0.wireOp",EDGE,"E15.sketch_text.stroke-77"),sQuery(id+"F0.wireOp",EDGE,"E15.sketch_text.stroke-78"),sQuery(id+"F0.wireOp",EDGE,"E15.sketch_text.stroke-79"),sQuery(id+"F0.wireOp",EDGE,"E15.sketch_text.stroke-80"),sQuery(id+"F0.wireOp",EDGE,"E15.sketch_text.stroke-81"),sQuery(id+"F0.wireOp",EDGE,"E15.sketch_text.stroke-82"),sQuery(id+"F0.wireOp",EDGE,"E15.sketch_text.stroke-83"),sQuery(id+"F0.wireOp",EDGE,"E15.sketch_text.stroke-84"),sQuery(id+"F0.wireOp",EDGE,"E15.sketch_text.stroke-85"),sQuery(id+"F0.wireOp",EDGE,"E15.sketch_text.stroke-86"),sQuery(id+"F0.wireOp",EDGE,"E15.sketch_text.stroke-87"),sQuery(id+"F0.wireOp",EDGE,"E15.sketch_text.stroke-88"),sQuery(id+"F0.wireOp",EDGE,"E15.sketch_text.stroke-89"),sQuery(id+"F0.wireOp",EDGE,"E15.sketch_text.stroke-90"),sQuery(id+"F0.wireOp",EDGE,"E15.sketch_text.stroke-91"),sQuery(id+"F0.wireOp",EDGE,"E15.sketch_text.stroke-92"),sQuery(id+"F0.wireOp",EDGE,"E15.sketch_text.stroke-93"),sQuery(id+"F0.wireOp",EDGE,"E15.sketch_text.stroke-94"),sQuery(id+"F0.wireOp",EDGE,"E15.sketch_text.stroke-95"),sQuery(id+"F0.wireOp",EDGE,"E15.sketch_text.stroke-101"),sQuery(id+"F0.wireOp",EDGE,"E15.sketch_text.stroke-102"),sQuery(id+"F0.wireOp",EDGE,"E15.sketch_text.stroke-103"),sQuery(id+"F0.wireOp",EDGE,"E15.sketch_text.stroke-104"),sQuery(id+"F0.wireOp",EDGE,"E15.sketch_text.stroke-105"),sQuery(id+"F0.wireOp",EDGE,"E15.sketch_text.stroke-106"),sQuery(id+"F0.wireOp",EDGE,"E15.sketch_text.stroke-107"),sQuery(id+"F0.wireOp",EDGE,"E15.sketch_text.stroke-108"),sQuery(id+"F0.wireOp",EDGE,"E15.sketch_text.stroke-109"),sQuery(id+"F0.wireOp",EDGE,"E15.sketch_text.stroke-110"),sQuery(id+"F0.wireOp",EDGE,"E15.sketch_text.stroke-111"),sQuery(id+"F0.wireOp",EDGE,"E15.sketch_text.stroke-112"),sQuery(id+"F0.wireOp",EDGE,"E15.sketch_text.stroke-113"),sQuery(id+"F0.wireOp",EDGE,"E15.sketch_text.stroke-114"),sQuery(id+"F0.wireOp",EDGE,"E15.sketch_text.stroke-115"),sQuery(id+"F0.wireOp",EDGE,"E15.sketch_text.stroke-116"),sQuery(id+"F0.wireOp",EDGE,"E15.sketch_text.stroke-117"),sQuery(id+"F0.wireOp",EDGE,"E15.sketch_text.stroke-118"),sQuery(id+"F0.wireOp",EDGE,"E15.sketch_text.stroke-119"),sQuery(id+"F0.wireOp",EDGE,"E15.sketch_text.stroke-120"),sQuery(id+"F0.wireOp",EDGE,"E15.sketch_text.stroke-121"),sQuery(id+"F0.wireOp",EDGE,"E15.sketch_text.stroke-122"),sQuery(id+"F0.wireOp",EDGE,"E15.sketch_text.stroke-123"),sQuery(id+"F0.wireOp",EDGE,"E15.sketch_text.stroke-124"),sQuery(id+"F0.wireOp",EDGE,"E15.sketch_text.stroke-125"),sQuery(id+"F0.wireOp",EDGE,"E15.sketch_text.stroke-126"),sQuery(id+"F0.wireOp",EDGE,"E15.sketch_text.stroke-127"),sQuery(id+"F0.wireOp",EDGE,"E15.sketch_text.stroke-128"),sQuery(id+"F0.wireOp",EDGE,"E15.sketch_text.stroke-129"),sQuery(id+"F0.wireOp",EDGE,"E15.sketch_text.stroke-130"),sQuery(id+"F0.wireOp",EDGE,"E15.sketch_text.stroke-131"),sQuery(id+"F0.wireOp",EDGE,"E15.sketch_text.stroke-132"),sQuery(id+"F0.wireOp",EDGE,"E15.sketch_text.stroke-133"),sQuery(id+"F0.wireOp",EDGE,"E15.sketch_text.stroke-134"),sQuery(id+"F0.wireOp",EDGE,"E15.sketch_text.stroke-135"),sQuery(id+"F0.wireOp",EDGE,"E15.sketch_text.stroke-136"),sQuery(id+"F0.wireOp",EDGE,"E15.sketch_text.stroke-137"),sQuery(id+"F0.wireOp",EDGE,"E15.sketch_text.stroke-138"),sQuery(id+"F0.wireOp",EDGE,"E15.sketch_text.stroke-139"),sQuery(id+"F0.wireOp",EDGE,"E15.sketch_text.stroke-140"),sQuery(id+"F0.wireOp",EDGE,"E15.sketch_text.stroke-141"),sQuery(id+"F0.wireOp",EDGE,"E15.sketch_text.stroke-142"),sQuery(id+"F0.wireOp",EDGE,"E15.sketch_text.stroke-143"),sQuery(id+"F0.wireOp",EDGE,"E15.sketch_text.stroke-144"),sQuery(id+"F0.wireOp",EDGE,"E15.sketch_text.stroke-145"),sQuery(id+"F0.wireOp",EDGE,"E15.sketch_text.stroke-146"),sQuery(id+"F0.wireOp",EDGE,"E15.sketch_text.stroke-147"),sQuery(id+"F0.wireOp",EDGE,"E15.sketch_text.stroke-148"),sQuery(id+"F0.wireOp",EDGE,"E15.sketch_text.stroke-149"),sQuery(id+"F0.wireOp",EDGE,"E15.sketch_text.stroke-150"),sQuery(id+"F0.wireOp",EDGE,"E15.sketch_text.stroke-151"),sQuery(id+"F0.wireOp",EDGE,"E15.sketch_text.stroke-152"),sQuery(id+"F0.wireOp",EDGE,"E15.sketch_text.stroke-153"),sQuery(id+"F0.wireOp",EDGE,"E15.sketch_text.stroke-154"),sQuery(id+"F0.wireOp",EDGE,"E15.sketch_text.stroke-155"),sQuery(id+"F0.wireOp",EDGE,"E15.sketch_text.stroke-156"),sQuery(id+"F0.wireOp",EDGE,"E15.sketch_text.stroke-157"),sQuery(id+"F0.wireOp",EDGE,"E15.sketch_text.stroke-158"),sQuery(id+"F0.wireOp",EDGE,"E15.sketch_text.stroke-159"),sQuery(id+"F0.wireOp",EDGE,"E15.sketch_text.stroke-160"),sQuery(id+"F0.wireOp",EDGE,"E15.sketch_text.stroke-161"),sQuery(id+"F0.wireOp",EDGE,"E16.bottom"),sQuery(id+"F0.wireOp",EDGE,"E17"),sQuery(id+"F0.wireOp",EDGE,"E19"),sQuery(id+"F0.wireOp",EDGE,"E21")])],"isStart":false})]});}
            fillet(context, id + "F10", {"entities" : qUnion([Q0]), "radius" : 2 * mm, "tangentPropagation" : true, "allowEdgeOverflow" : false});
        }
    });
